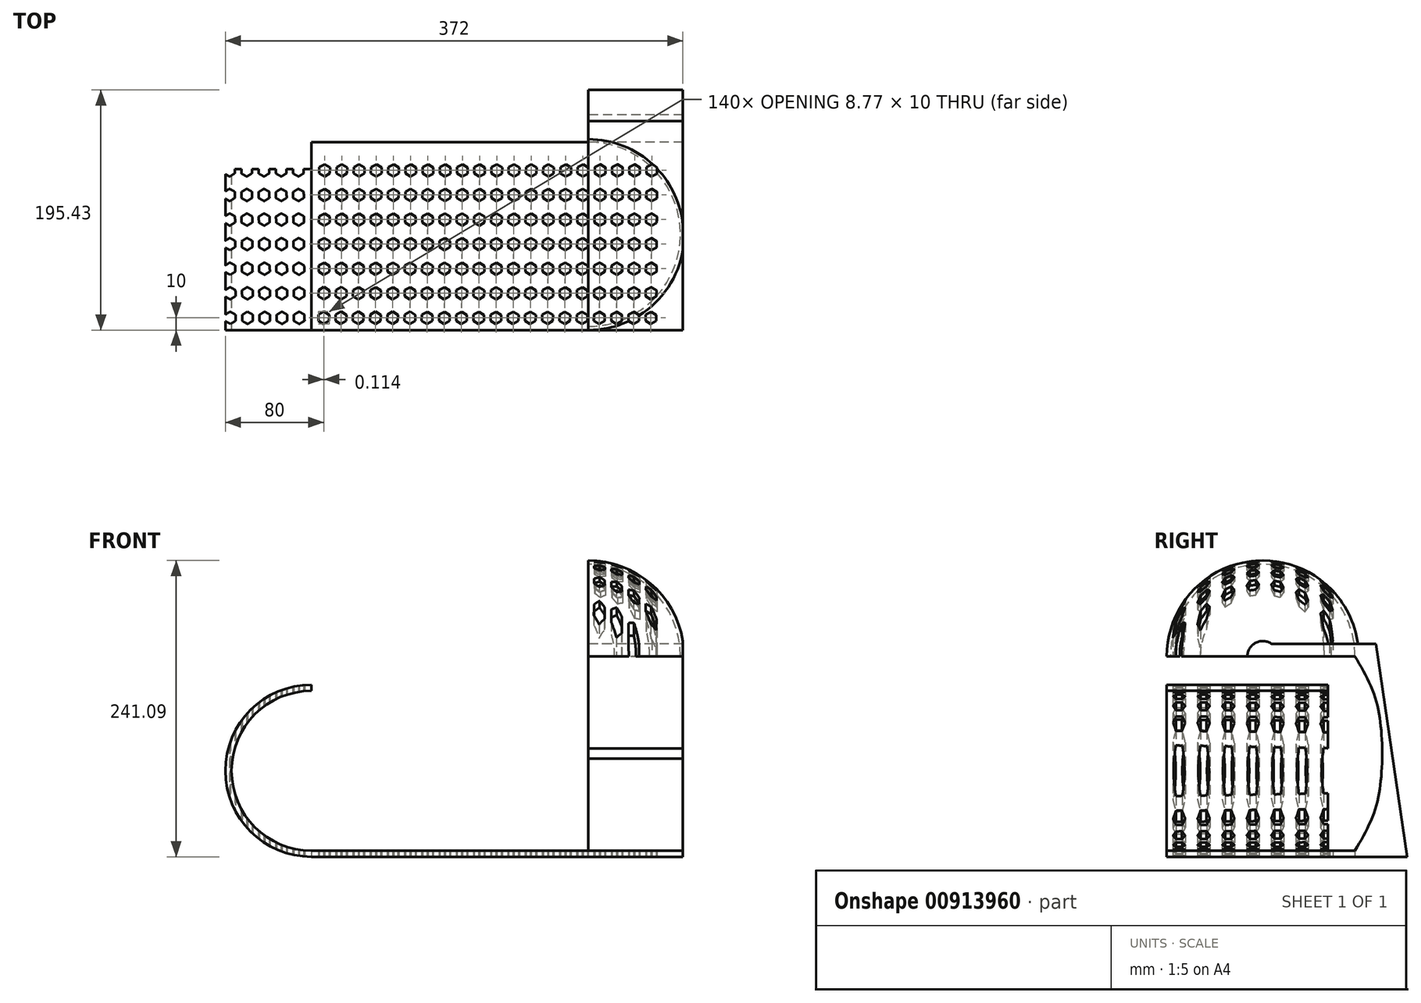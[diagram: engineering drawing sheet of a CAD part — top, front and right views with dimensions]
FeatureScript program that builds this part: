
annotation { "Feature Type Name" : "Feature", "Feature Type Description" : "" }
export const myFeature = defineFeature(function(context is Context, id is Id, definition is map)
    precondition{}
    {
        {
            var Q0;
            Q0=qCreatedBy(makeId("Right.planeOp"),FACE);
            var sketch = newSketch(context, id + "F0", { "sketchPlane" : qUnion([Q0])});
            skArc(sketch, "E0", {"start": v(75, 0) * mm, "mid": v(0, 75) * mm, "end": v(-75, 0) * mm});
            skLineSegment(sketch, "E1", {"start": v(-75, 0) * mm, "end": v(75, 0) * mm, "construction": true});
            skArc(sketch, "E2.0", {"start": v(78, 0) * mm, "mid": v(0, 78) * mm, "end": v(-78, 0) * mm});
            skLineSegment(sketch, "E3", {"start": v(-78, 0) * mm, "end": v(-75, 0) * mm});
            skLineSegment(sketch, "E4", {"start": v(75, 0) * mm, "end": v(78, 0) * mm});
            skSolve(sketch);
        }
        {
            var Q0;
            Q0=makeQuery(id+"F0.imprint","IMPRINT",FACE,{"disambiguationData":[TD([[makeQuery(id+"F0.imprint","IMPRINT",EDGE,{"derivedFrom":sQuery(id+"F0.wireOp",EDGE,"E0")}),-1.0]])]});
            var Q1;
            Q1=sQuery(id+"F0.wireOp",EDGE,"E1");
            revolve(context, id + "F1", {"surfaceOperationType" : NewSurfaceOperationType.NEW, "entities" : qUnion([Q0]), "axis" : qUnion([Q1]), "revolveType" : RevolveType.ONE_DIRECTION, "angle" : 90 * degree});
        }
        {
            var Q0;
            Q0=qCreatedBy(makeId("Right.planeOp"),FACE);
            var sketch = newSketch(context, id + "F2", { "sketchPlane" : qUnion([Q0])});
            skLineSegment(sketch, "E5.0.0", {"start": v(75, 0) * mm, "end": v(-75, 0) * mm});
            skArc(sketch, "E6", {"start": v(75, 0) * mm, "mid": v(0, 75) * mm, "end": v(-75, 0) * mm, "construction": true});
            skFitSpline(sketch, "E7", {"points": [v(75, 0) * mm, v(91.76, -34.74) * mm, v(97.2, -75) * mm], "startDerivative": vector(40.46, -68.62) * mm, "endDerivative": vector(3.7, -86.55) * mm});
            skLineSegment(sketch, "E8", {"start": v(92, 10) * mm, "end": v(105.08, -79.04) * mm});
            skLineSegment(sketch, "E9", {"start": v(105.08, -79.04) * mm, "end": v(97.2, -75) * mm});
            skArc(sketch, "E10.0.0", {"start": v(78, 0) * mm, "mid": v(0, 78) * mm, "end": v(-78, 0) * mm, "construction": true});
            skLineSegment(sketch, "E10.0.1", {"start": v(-78, 0) * mm, "end": v(78, 0) * mm});
            skLineSegment(sketch, "E11", {"start": v(-78, 0) * mm, "end": v(-78, 10) * mm});
            skLineSegment(sketch, "E12", {"start": v(-78, 10) * mm, "end": v(92, 10) * mm});
            skLineSegment(sketch, "E13", {"start": v(75, 0) * mm, "end": v(75, 10) * mm});
            skLineSegment(sketch, "E14", {"start": v(105.08, -79.04) * mm, "end": v(-109.24, -79.04) * mm, "construction": true});
            skFitSpline(sketch, "E15.MirrorCS", {"points": [v(75, -158.09) * mm, v(91.76, -123.35) * mm, v(97.2, -83.09) * mm], "startDerivative": vector(40.46, 68.62) * mm, "endDerivative": vector(3.7, 86.55) * mm});
            skLineSegment(sketch, "E16", {"start": v(105.08, -79.04) * mm, "end": v(117.43, -163.09) * mm});
            skLineSegment(sketch, "E17", {"start": v(117.43, -163.09) * mm, "end": v(-78, -163.09) * mm});
            skLineSegment(sketch, "E18", {"start": v(-78, -163.09) * mm, "end": v(-78, 0) * mm, "construction": true});
            skLineSegment(sketch, "E19", {"start": v(75, -158.09) * mm, "end": v(-78, -158.09) * mm});
            skLineSegment(sketch, "E20", {"start": v(-78, -158.09) * mm, "end": v(-78, -163.09) * mm});
            skLineSegment(sketch, "E21", {"start": v(97.2, -83.09) * mm, "end": v(97.2, -75) * mm});
            skLineSegment(sketch, "E22", {"start": v(75, -158.09) * mm, "end": v(75, -163.09) * mm});
            skSolve(sketch);
        }
        {
            var Q0;
            {var subQ1=sQuery(id+"F2.wireOp",EDGE,"E7");Q0=makeQuery(id+"F2.imprint","IMPRINT",FACE,{"disambiguationData":[TD([[makeQuery(id+"F2.imprint","IMPRINT",EDGE,{"derivedFrom":subQ1}),1.0]])]});}
            extrude(context, id + "F3", {"entities" : qUnion([Q0]), "depth" : 150 * mm, "offsetDistance" : 25 * mm, "hasSecondDirection" : true, "secondDirectionOppositeDirection" : true, "secondDirectionDepth" : 0 * mm});
        }
        {
            var Q0;
            Q0=makeQuery(id+"F2.imprint","IMPRINT",FACE,{"disambiguationData":[TD([[makeQuery(id+"F2.imprint","IMPRINT",EDGE,{"derivedFrom":sQuery(id+"F2.wireOp",EDGE,"E9")}),1.0]])]});
            var Q1;
            Q1=makeQuery(id+"F2.imprint","IMPRINT",FACE,{"disambiguationData":[TD([[makeQuery(id+"F2.imprint","IMPRINT",EDGE,{"derivedFrom":sQuery(id+"F2.wireOp",EDGE,"E19")}),1.0]])]});
            extrude(context, id + "F4", {"entities" : qUnion([Q0, Q1]), "operationType" : NewBodyOperationType.ADD, "depth" : 77 * mm, "offsetDistance" : 25 * mm});
        }
        {
            var Q0;
            Q0=makeQuery(id+"F3.opExtrude","CAP_FACE",FACE,{"disambiguationData":[OSD([sQuery(id+"F2.wireOp",EDGE,"E7"),sQuery(id+"F2.wireOp",EDGE,"E8"),sQuery(id+"F2.wireOp",EDGE,"E9"),sQuery(id+"F2.wireOp",EDGE,"E12"),sQuery(id+"F2.wireOp",EDGE,"E13")])],"isStart":false});
            var sketch = newSketch(context, id + "F5", { "sketchPlane" : qUnion([Q0])});
            skLineSegment(sketch, "E23.bottom", {"start": v(0, 0) * mm, "end": v(75, 0) * mm});
            skLineSegment(sketch, "E23.top", {"start": v(0, 10) * mm, "end": v(75, 10) * mm});
            skLineSegment(sketch, "E23.left", {"start": v(0, 0) * mm, "end": v(0, 10) * mm});
            skLineSegment(sketch, "E23.right", {"start": v(75, 0) * mm, "end": v(75, 10) * mm});
            skSolve(sketch);
        }
        {
            var Q0;
            Q0=makeQuery(id+"F5.imprint","IMPRINT",FACE,{"disambiguationData":[TD([[makeQuery(id+"F5.imprint","IMPRINT",EDGE,{"derivedFrom":sQuery(id+"F5.wireOp",EDGE,"E23.bottom")}),1.0]])]});
            extrude(context, id + "F6", {"entities" : qUnion([Q0]), "operationType" : NewBodyOperationType.ADD, "endBound" : BoundingType.UP_TO_NEXT, "oppositeDirection" : true, "depth" : 25 * mm, "offsetDistance" : 25 * mm});
        }
        {
            var Q0;
            Q0=makeQuery(id+"F4.opExtrude","CAP_FACE",FACE,{"disambiguationData":[OSD([sQuery(id+"F2.wireOp",EDGE,"E9"),sQuery(id+"F2.wireOp",EDGE,"E15.MirrorCS"),sQuery(id+"F2.wireOp",EDGE,"E16"),sQuery(id+"F2.wireOp",EDGE,"E17"),sQuery(id+"F2.wireOp",EDGE,"E19"),sQuery(id+"F2.wireOp",EDGE,"E20"),sQuery(id+"F2.wireOp",EDGE,"E21")])],"isStart":true});
            var sketch = newSketch(context, id + "F7", { "sketchPlane" : qUnion([Q0])});
            skLineSegment(sketch, "E24.bottom", {"start": v(-75, -158.09) * mm, "end": v(78, -158.09) * mm});
            skLineSegment(sketch, "E24.top", {"start": v(-75, -163.09) * mm, "end": v(78, -163.09) * mm});
            skLineSegment(sketch, "E24.left", {"start": v(-75, -158.09) * mm, "end": v(-75, -163.09) * mm});
            skLineSegment(sketch, "E24.right", {"start": v(78, -158.09) * mm, "end": v(78, -163.09) * mm});
            skSolve(sketch);
        }
        {
            var Q0;
            Q0=makeQuery(id+"F7.imprint","IMPRINT",FACE,{"disambiguationData":[TD([[makeQuery(id+"F7.imprint","IMPRINT",EDGE,{"derivedFrom":sQuery(id+"F7.wireOp",EDGE,"E24.bottom")}),-1.0]])]});
            extrude(context, id + "F8", {"entities" : qUnion([Q0]), "operationType" : NewBodyOperationType.ADD, "depth" : 225 * mm, "offsetDistance" : 25 * mm});
        }
        {
            var Q0;
            Q0=makeQuery(id+"F8.boolean.opBoolean","MERGE",FACE,{"derivedFrom":[makeQuery(id+"F4.opExtrude","SWEPT_FACE",FACE,{"disambiguationData":[OSD([sQuery(id+"F2.wireOp",EDGE,"E20")])]}),makeQuery(id+"F8.opExtrude","SWEPT_FACE",FACE,{"disambiguationData":[OSD([sQuery(id+"F7.wireOp",EDGE,"E24.right")])]})]});
            var sketch = newSketch(context, id + "F9", { "sketchPlane" : qUnion([Q0])});
            skArc(sketch, "E25", {"start": v(-225, -28.09) * mm, "mid": v(-290, -93.09) * mm, "end": v(-225, -158.09) * mm});
            skArc(sketch, "E26.0", {"start": v(-225, -23.09) * mm, "mid": v(-295, -93.09) * mm, "end": v(-225, -163.09) * mm});
            skLineSegment(sketch, "E27", {"start": v(-225, -28.09) * mm, "end": v(-225, -23.09) * mm});
            skSolve(sketch);
        }
        {
            var Q0;
            Q0 = qSketchRegion(id + "F9", true);
            var Q1;
            Q1=makeQuery(id+"F9.imprint","IMPRINT",FACE,{"disambiguationData":[TD([[makeQuery(id+"F9.imprint","IMPRINT",EDGE,{"derivedFrom":sQuery(id+"F9.wireOp",EDGE,"E25")}),-1.0]])]});
            extrude(context, id + "F10", {"entities" : qUnion([Q0, Q1]), "operationType" : NewBodyOperationType.ADD, "oppositeDirection" : true, "depth" : 131 * mm, "offsetDistance" : 25 * mm});
        }
        {
            var Q0;
            Q0=makeQuery(id+"F8.boolean.opBoolean","MERGE",FACE,{"derivedFrom":[makeQuery(id+"F4.opExtrude","SWEPT_FACE",FACE,{"disambiguationData":[OSD([sQuery(id+"F2.wireOp",EDGE,"E17")])]}),makeQuery(id+"F8.opExtrude","SWEPT_FACE",FACE,{"disambiguationData":[OSD([sQuery(id+"F7.wireOp",EDGE,"E24.top")])]})]});
            var sketch = newSketch(context, id + "F11", { "sketchPlane" : qUnion([Q0])});
            skCircle(sketch, "E28.cCircle", {"center": v(-215, 68) * mm, "radius": 4.33 * mm, "construction": true});
            skLineSegment(sketch, "E28.0", {"start": v(-210.61, 65.6) * mm, "end": v(-214.89, 63) * mm});
            skLineSegment(sketch, "E28.1", {"start": v(-214.89, 63) * mm, "end": v(-219.27, 65.4) * mm});
            skLineSegment(sketch, "E28.2", {"start": v(-219.27, 65.4) * mm, "end": v(-219.39, 70.4) * mm});
            skLineSegment(sketch, "E28.3", {"start": v(-219.39, 70.4) * mm, "end": v(-215.11, 73) * mm});
            skLineSegment(sketch, "E28.4", {"start": v(-215.11, 73) * mm, "end": v(-210.73, 70.6) * mm});
            skLineSegment(sketch, "E28.5", {"start": v(-210.73, 70.6) * mm, "end": v(-210.61, 65.6) * mm});
            skPoint(sketch, "E28.0.midPoint", {"position": v(-212.75, 64.3) * mm});
            skLineSegment(sketch, "E29.0.1.0", {"start": v(-215, 53) * mm, "end": v(-210.61, 50.6) * mm});
            skLineSegment(sketch, "E29.0.1.1", {"start": v(-210.61, 50.6) * mm, "end": v(-210.5, 45.6) * mm});
            skLineSegment(sketch, "E29.0.1.2", {"start": v(-219.27, 50.4) * mm, "end": v(-215, 53) * mm});
            skLineSegment(sketch, "E29.0.1.3", {"start": v(-219.16, 45.4) * mm, "end": v(-219.27, 50.4) * mm});
            skLineSegment(sketch, "E29.0.1.4", {"start": v(-214.77, 43) * mm, "end": v(-219.16, 45.4) * mm});
            skLineSegment(sketch, "E29.0.1.5", {"start": v(-210.5, 45.6) * mm, "end": v(-214.77, 43) * mm});
            skLineSegment(sketch, "E29.0.2.0", {"start": v(-214.89, 33) * mm, "end": v(-210.5, 30.6) * mm});
            skLineSegment(sketch, "E29.0.2.1", {"start": v(-210.5, 30.6) * mm, "end": v(-210.38, 25.6) * mm});
            skLineSegment(sketch, "E29.0.2.2", {"start": v(-219.16, 30.4) * mm, "end": v(-214.89, 33) * mm});
            skLineSegment(sketch, "E29.0.2.3", {"start": v(-219.04, 25.4) * mm, "end": v(-219.16, 30.4) * mm});
            skLineSegment(sketch, "E29.0.2.4", {"start": v(-214.66, 23) * mm, "end": v(-219.04, 25.4) * mm});
            skLineSegment(sketch, "E29.0.2.5", {"start": v(-210.38, 25.6) * mm, "end": v(-214.66, 23) * mm});
            skLineSegment(sketch, "E29.0.3.0", {"start": v(-214.77, 13) * mm, "end": v(-210.38, 10.6) * mm});
            skLineSegment(sketch, "E29.0.3.1", {"start": v(-210.38, 10.6) * mm, "end": v(-210.27, 5.6) * mm});
            skLineSegment(sketch, "E29.0.3.2", {"start": v(-219.04, 10.4) * mm, "end": v(-214.77, 13) * mm});
            skLineSegment(sketch, "E29.0.3.3", {"start": v(-218.93, 5.4) * mm, "end": v(-219.04, 10.4) * mm});
            skLineSegment(sketch, "E29.0.3.4", {"start": v(-214.54, 3) * mm, "end": v(-218.93, 5.4) * mm});
            skLineSegment(sketch, "E29.0.3.5", {"start": v(-210.27, 5.6) * mm, "end": v(-214.54, 3) * mm});
            skLineSegment(sketch, "E29.0.4.0", {"start": v(-214.66, -7) * mm, "end": v(-210.27, -9.4) * mm});
            skLineSegment(sketch, "E29.0.4.1", {"start": v(-210.27, -9.4) * mm, "end": v(-210.16, -14.4) * mm});
            skLineSegment(sketch, "E29.0.4.2", {"start": v(-218.93, -9.6) * mm, "end": v(-214.66, -7) * mm});
            skLineSegment(sketch, "E29.0.4.3", {"start": v(-218.81, -14.6) * mm, "end": v(-218.93, -9.6) * mm});
            skLineSegment(sketch, "E29.0.4.4", {"start": v(-214.43, -17) * mm, "end": v(-218.81, -14.6) * mm});
            skLineSegment(sketch, "E29.0.4.5", {"start": v(-210.16, -14.4) * mm, "end": v(-214.43, -17) * mm});
            skLineSegment(sketch, "E29.0.5.0", {"start": v(-214.54, -27) * mm, "end": v(-210.16, -29.4) * mm});
            skLineSegment(sketch, "E29.0.5.1", {"start": v(-210.16, -29.4) * mm, "end": v(-210.04, -34.4) * mm});
            skLineSegment(sketch, "E29.0.5.2", {"start": v(-218.81, -29.6) * mm, "end": v(-214.54, -27) * mm});
            skLineSegment(sketch, "E29.0.5.3", {"start": v(-218.7, -34.6) * mm, "end": v(-218.81, -29.6) * mm});
            skLineSegment(sketch, "E29.0.5.4", {"start": v(-214.31, -37) * mm, "end": v(-218.7, -34.6) * mm});
            skLineSegment(sketch, "E29.0.5.5", {"start": v(-210.04, -34.4) * mm, "end": v(-214.31, -37) * mm});
            skLineSegment(sketch, "E29.0.6.0", {"start": v(-214.43, -47) * mm, "end": v(-210.04, -49.4) * mm});
            skLineSegment(sketch, "E29.0.6.1", {"start": v(-210.04, -49.4) * mm, "end": v(-209.93, -54.4) * mm});
            skLineSegment(sketch, "E29.0.6.2", {"start": v(-218.7, -49.6) * mm, "end": v(-214.43, -47) * mm});
            skLineSegment(sketch, "E29.0.6.3", {"start": v(-218.59, -54.6) * mm, "end": v(-218.7, -49.6) * mm});
            skLineSegment(sketch, "E29.0.6.4", {"start": v(-214.2, -57) * mm, "end": v(-218.59, -54.6) * mm});
            skLineSegment(sketch, "E29.0.6.5", {"start": v(-209.93, -54.4) * mm, "end": v(-214.2, -57) * mm});
            skLineSegment(sketch, "E29.1.0.0", {"start": v(-201.11, 73) * mm, "end": v(-196.73, 70.6) * mm});
            skLineSegment(sketch, "E29.1.0.1", {"start": v(-196.73, 70.6) * mm, "end": v(-196.61, 65.6) * mm});
            skLineSegment(sketch, "E29.1.0.2", {"start": v(-205.39, 70.4) * mm, "end": v(-201.11, 73) * mm});
            skLineSegment(sketch, "E29.1.0.3", {"start": v(-205.27, 65.4) * mm, "end": v(-205.39, 70.4) * mm});
            skLineSegment(sketch, "E29.1.0.4", {"start": v(-200.89, 63) * mm, "end": v(-205.27, 65.4) * mm});
            skLineSegment(sketch, "E29.1.0.5", {"start": v(-196.61, 65.6) * mm, "end": v(-200.89, 63) * mm});
            skLineSegment(sketch, "E29.1.1.0", {"start": v(-201, 53) * mm, "end": v(-196.61, 50.6) * mm});
            skLineSegment(sketch, "E29.1.1.1", {"start": v(-196.61, 50.6) * mm, "end": v(-196.5, 45.6) * mm});
            skLineSegment(sketch, "E29.1.1.2", {"start": v(-205.27, 50.4) * mm, "end": v(-201, 53) * mm});
            skLineSegment(sketch, "E29.1.1.3", {"start": v(-205.16, 45.4) * mm, "end": v(-205.27, 50.4) * mm});
            skLineSegment(sketch, "E29.1.1.4", {"start": v(-200.77, 43) * mm, "end": v(-205.16, 45.4) * mm});
            skLineSegment(sketch, "E29.1.1.5", {"start": v(-196.5, 45.6) * mm, "end": v(-200.77, 43) * mm});
            skLineSegment(sketch, "E29.1.2.0", {"start": v(-200.89, 33) * mm, "end": v(-196.5, 30.6) * mm});
            skLineSegment(sketch, "E29.1.2.1", {"start": v(-196.5, 30.6) * mm, "end": v(-196.38, 25.6) * mm});
            skLineSegment(sketch, "E29.1.2.2", {"start": v(-205.16, 30.4) * mm, "end": v(-200.89, 33) * mm});
            skLineSegment(sketch, "E29.1.2.3", {"start": v(-205.04, 25.4) * mm, "end": v(-205.16, 30.4) * mm});
            skLineSegment(sketch, "E29.1.2.4", {"start": v(-200.66, 23) * mm, "end": v(-205.04, 25.4) * mm});
            skLineSegment(sketch, "E29.1.2.5", {"start": v(-196.38, 25.6) * mm, "end": v(-200.66, 23) * mm});
            skLineSegment(sketch, "E29.1.3.0", {"start": v(-200.77, 13) * mm, "end": v(-196.38, 10.6) * mm});
            skLineSegment(sketch, "E29.1.3.1", {"start": v(-196.38, 10.6) * mm, "end": v(-196.27, 5.6) * mm});
            skLineSegment(sketch, "E29.1.3.2", {"start": v(-205.04, 10.4) * mm, "end": v(-200.77, 13) * mm});
            skLineSegment(sketch, "E29.1.3.3", {"start": v(-204.93, 5.4) * mm, "end": v(-205.04, 10.4) * mm});
            skLineSegment(sketch, "E29.1.3.4", {"start": v(-200.54, 3) * mm, "end": v(-204.93, 5.4) * mm});
            skLineSegment(sketch, "E29.1.3.5", {"start": v(-196.27, 5.6) * mm, "end": v(-200.54, 3) * mm});
            skLineSegment(sketch, "E29.1.4.0", {"start": v(-200.66, -7) * mm, "end": v(-196.27, -9.4) * mm});
            skLineSegment(sketch, "E29.1.4.1", {"start": v(-196.27, -9.4) * mm, "end": v(-196.16, -14.4) * mm});
            skLineSegment(sketch, "E29.1.4.2", {"start": v(-204.93, -9.6) * mm, "end": v(-200.66, -7) * mm});
            skLineSegment(sketch, "E29.1.4.3", {"start": v(-204.81, -14.6) * mm, "end": v(-204.93, -9.6) * mm});
            skLineSegment(sketch, "E29.1.4.4", {"start": v(-200.43, -17) * mm, "end": v(-204.81, -14.6) * mm});
            skLineSegment(sketch, "E29.1.4.5", {"start": v(-196.16, -14.4) * mm, "end": v(-200.43, -17) * mm});
            skLineSegment(sketch, "E29.1.5.0", {"start": v(-200.54, -27) * mm, "end": v(-196.16, -29.4) * mm});
            skLineSegment(sketch, "E29.1.5.1", {"start": v(-196.16, -29.4) * mm, "end": v(-196.04, -34.4) * mm});
            skLineSegment(sketch, "E29.1.5.2", {"start": v(-204.81, -29.6) * mm, "end": v(-200.54, -27) * mm});
            skLineSegment(sketch, "E29.1.5.3", {"start": v(-204.7, -34.6) * mm, "end": v(-204.81, -29.6) * mm});
            skLineSegment(sketch, "E29.1.5.4", {"start": v(-200.31, -37) * mm, "end": v(-204.7, -34.6) * mm});
            skLineSegment(sketch, "E29.1.5.5", {"start": v(-196.04, -34.4) * mm, "end": v(-200.31, -37) * mm});
            skLineSegment(sketch, "E29.1.6.0", {"start": v(-200.43, -47) * mm, "end": v(-196.04, -49.4) * mm});
            skLineSegment(sketch, "E29.1.6.1", {"start": v(-196.04, -49.4) * mm, "end": v(-195.93, -54.4) * mm});
            skLineSegment(sketch, "E29.1.6.2", {"start": v(-204.7, -49.6) * mm, "end": v(-200.43, -47) * mm});
            skLineSegment(sketch, "E29.1.6.3", {"start": v(-204.59, -54.59) * mm, "end": v(-204.7, -49.6) * mm});
            skLineSegment(sketch, "E29.1.6.4", {"start": v(-200.2, -56.99) * mm, "end": v(-204.59, -54.59) * mm});
            skLineSegment(sketch, "E29.1.6.5", {"start": v(-195.93, -54.4) * mm, "end": v(-200.2, -56.99) * mm});
            skLineSegment(sketch, "E29.2.0.0", {"start": v(-187.11, 73) * mm, "end": v(-182.73, 70.6) * mm});
            skLineSegment(sketch, "E29.2.0.1", {"start": v(-182.73, 70.6) * mm, "end": v(-182.61, 65.6) * mm});
            skLineSegment(sketch, "E29.2.0.2", {"start": v(-191.39, 70.4) * mm, "end": v(-187.11, 73) * mm});
            skLineSegment(sketch, "E29.2.0.3", {"start": v(-191.27, 65.4) * mm, "end": v(-191.39, 70.4) * mm});
            skLineSegment(sketch, "E29.2.0.4", {"start": v(-186.89, 63) * mm, "end": v(-191.27, 65.4) * mm});
            skLineSegment(sketch, "E29.2.0.5", {"start": v(-182.61, 65.6) * mm, "end": v(-186.89, 63) * mm});
            skLineSegment(sketch, "E29.2.1.0", {"start": v(-187, 53) * mm, "end": v(-182.61, 50.6) * mm});
            skLineSegment(sketch, "E29.2.1.1", {"start": v(-182.61, 50.6) * mm, "end": v(-182.5, 45.6) * mm});
            skLineSegment(sketch, "E29.2.1.2", {"start": v(-191.27, 50.4) * mm, "end": v(-187, 53) * mm});
            skLineSegment(sketch, "E29.2.1.3", {"start": v(-191.16, 45.4) * mm, "end": v(-191.27, 50.4) * mm});
            skLineSegment(sketch, "E29.2.1.4", {"start": v(-186.77, 43) * mm, "end": v(-191.16, 45.4) * mm});
            skLineSegment(sketch, "E29.2.1.5", {"start": v(-182.5, 45.6) * mm, "end": v(-186.77, 43) * mm});
            skLineSegment(sketch, "E29.2.2.0", {"start": v(-186.89, 33) * mm, "end": v(-182.5, 30.6) * mm});
            skLineSegment(sketch, "E29.2.2.1", {"start": v(-182.5, 30.6) * mm, "end": v(-182.38, 25.6) * mm});
            skLineSegment(sketch, "E29.2.2.2", {"start": v(-191.16, 30.4) * mm, "end": v(-186.89, 33) * mm});
            skLineSegment(sketch, "E29.2.2.3", {"start": v(-191.04, 25.4) * mm, "end": v(-191.16, 30.4) * mm});
            skLineSegment(sketch, "E29.2.2.4", {"start": v(-186.66, 23) * mm, "end": v(-191.04, 25.4) * mm});
            skLineSegment(sketch, "E29.2.2.5", {"start": v(-182.38, 25.6) * mm, "end": v(-186.66, 23) * mm});
            skLineSegment(sketch, "E29.2.3.0", {"start": v(-186.77, 13) * mm, "end": v(-182.38, 10.6) * mm});
            skLineSegment(sketch, "E29.2.3.1", {"start": v(-182.38, 10.6) * mm, "end": v(-182.27, 5.6) * mm});
            skLineSegment(sketch, "E29.2.3.2", {"start": v(-191.04, 10.4) * mm, "end": v(-186.77, 13) * mm});
            skLineSegment(sketch, "E29.2.3.3", {"start": v(-190.93, 5.4) * mm, "end": v(-191.04, 10.4) * mm});
            skLineSegment(sketch, "E29.2.3.4", {"start": v(-186.54, 3) * mm, "end": v(-190.93, 5.4) * mm});
            skLineSegment(sketch, "E29.2.3.5", {"start": v(-182.27, 5.6) * mm, "end": v(-186.54, 3) * mm});
            skLineSegment(sketch, "E29.2.4.0", {"start": v(-186.66, -7) * mm, "end": v(-182.27, -9.4) * mm});
            skLineSegment(sketch, "E29.2.4.1", {"start": v(-182.27, -9.4) * mm, "end": v(-182.16, -14.4) * mm});
            skLineSegment(sketch, "E29.2.4.2", {"start": v(-190.93, -9.6) * mm, "end": v(-186.66, -7) * mm});
            skLineSegment(sketch, "E29.2.4.3", {"start": v(-190.81, -14.6) * mm, "end": v(-190.93, -9.6) * mm});
            skLineSegment(sketch, "E29.2.4.4", {"start": v(-186.43, -17) * mm, "end": v(-190.81, -14.6) * mm});
            skLineSegment(sketch, "E29.2.4.5", {"start": v(-182.16, -14.4) * mm, "end": v(-186.43, -17) * mm});
            skLineSegment(sketch, "E29.2.5.0", {"start": v(-186.54, -27) * mm, "end": v(-182.16, -29.4) * mm});
            skLineSegment(sketch, "E29.2.5.1", {"start": v(-182.16, -29.4) * mm, "end": v(-182.04, -34.4) * mm});
            skLineSegment(sketch, "E29.2.5.2", {"start": v(-190.81, -29.6) * mm, "end": v(-186.54, -27) * mm});
            skLineSegment(sketch, "E29.2.5.3", {"start": v(-190.7, -34.6) * mm, "end": v(-190.81, -29.6) * mm});
            skLineSegment(sketch, "E29.2.5.4", {"start": v(-186.31, -37) * mm, "end": v(-190.7, -34.6) * mm});
            skLineSegment(sketch, "E29.2.5.5", {"start": v(-182.04, -34.4) * mm, "end": v(-186.31, -37) * mm});
            skLineSegment(sketch, "E29.2.6.0", {"start": v(-186.43, -47) * mm, "end": v(-182.04, -49.4) * mm});
            skLineSegment(sketch, "E29.2.6.1", {"start": v(-182.04, -49.4) * mm, "end": v(-181.93, -54.4) * mm});
            skLineSegment(sketch, "E29.2.6.2", {"start": v(-190.7, -49.6) * mm, "end": v(-186.43, -47) * mm});
            skLineSegment(sketch, "E29.2.6.3", {"start": v(-190.59, -54.59) * mm, "end": v(-190.7, -49.6) * mm});
            skLineSegment(sketch, "E29.2.6.4", {"start": v(-186.2, -56.99) * mm, "end": v(-190.59, -54.59) * mm});
            skLineSegment(sketch, "E29.2.6.5", {"start": v(-181.93, -54.4) * mm, "end": v(-186.2, -56.99) * mm});
            skLineSegment(sketch, "E29.3.0.0", {"start": v(-173.11, 73) * mm, "end": v(-168.73, 70.6) * mm});
            skLineSegment(sketch, "E29.3.0.1", {"start": v(-168.73, 70.6) * mm, "end": v(-168.61, 65.6) * mm});
            skLineSegment(sketch, "E29.3.0.2", {"start": v(-177.39, 70.4) * mm, "end": v(-173.11, 73) * mm});
            skLineSegment(sketch, "E29.3.0.3", {"start": v(-177.27, 65.4) * mm, "end": v(-177.39, 70.4) * mm});
            skLineSegment(sketch, "E29.3.0.4", {"start": v(-172.89, 63) * mm, "end": v(-177.27, 65.4) * mm});
            skLineSegment(sketch, "E29.3.0.5", {"start": v(-168.61, 65.6) * mm, "end": v(-172.89, 63) * mm});
            skLineSegment(sketch, "E29.3.1.0", {"start": v(-173, 53) * mm, "end": v(-168.61, 50.6) * mm});
            skLineSegment(sketch, "E29.3.1.1", {"start": v(-168.61, 50.6) * mm, "end": v(-168.5, 45.6) * mm});
            skLineSegment(sketch, "E29.3.1.2", {"start": v(-177.27, 50.4) * mm, "end": v(-173, 53) * mm});
            skLineSegment(sketch, "E29.3.1.3", {"start": v(-177.16, 45.4) * mm, "end": v(-177.27, 50.4) * mm});
            skLineSegment(sketch, "E29.3.1.4", {"start": v(-172.77, 43) * mm, "end": v(-177.16, 45.4) * mm});
            skLineSegment(sketch, "E29.3.1.5", {"start": v(-168.5, 45.6) * mm, "end": v(-172.77, 43) * mm});
            skLineSegment(sketch, "E29.3.2.0", {"start": v(-172.89, 33) * mm, "end": v(-168.5, 30.6) * mm});
            skLineSegment(sketch, "E29.3.2.1", {"start": v(-168.5, 30.6) * mm, "end": v(-168.38, 25.6) * mm});
            skLineSegment(sketch, "E29.3.2.2", {"start": v(-177.16, 30.4) * mm, "end": v(-172.89, 33) * mm});
            skLineSegment(sketch, "E29.3.2.3", {"start": v(-177.04, 25.4) * mm, "end": v(-177.16, 30.4) * mm});
            skLineSegment(sketch, "E29.3.2.4", {"start": v(-172.66, 23) * mm, "end": v(-177.04, 25.4) * mm});
            skLineSegment(sketch, "E29.3.2.5", {"start": v(-168.38, 25.6) * mm, "end": v(-172.66, 23) * mm});
            skLineSegment(sketch, "E29.3.3.0", {"start": v(-172.77, 13) * mm, "end": v(-168.38, 10.6) * mm});
            skLineSegment(sketch, "E29.3.3.1", {"start": v(-168.38, 10.6) * mm, "end": v(-168.27, 5.6) * mm});
            skLineSegment(sketch, "E29.3.3.2", {"start": v(-177.04, 10.4) * mm, "end": v(-172.77, 13) * mm});
            skLineSegment(sketch, "E29.3.3.3", {"start": v(-176.93, 5.4) * mm, "end": v(-177.04, 10.4) * mm});
            skLineSegment(sketch, "E29.3.3.4", {"start": v(-172.54, 3) * mm, "end": v(-176.93, 5.4) * mm});
            skLineSegment(sketch, "E29.3.3.5", {"start": v(-168.27, 5.6) * mm, "end": v(-172.54, 3) * mm});
            skLineSegment(sketch, "E29.3.4.0", {"start": v(-172.66, -7) * mm, "end": v(-168.27, -9.4) * mm});
            skLineSegment(sketch, "E29.3.4.1", {"start": v(-168.27, -9.4) * mm, "end": v(-168.16, -14.4) * mm});
            skLineSegment(sketch, "E29.3.4.2", {"start": v(-176.93, -9.6) * mm, "end": v(-172.66, -7) * mm});
            skLineSegment(sketch, "E29.3.4.3", {"start": v(-176.81, -14.6) * mm, "end": v(-176.93, -9.6) * mm});
            skLineSegment(sketch, "E29.3.4.4", {"start": v(-172.43, -17) * mm, "end": v(-176.81, -14.6) * mm});
            skLineSegment(sketch, "E29.3.4.5", {"start": v(-168.16, -14.4) * mm, "end": v(-172.43, -17) * mm});
            skLineSegment(sketch, "E29.3.5.0", {"start": v(-172.54, -27) * mm, "end": v(-168.16, -29.4) * mm});
            skLineSegment(sketch, "E29.3.5.1", {"start": v(-168.16, -29.4) * mm, "end": v(-168.04, -34.4) * mm});
            skLineSegment(sketch, "E29.3.5.2", {"start": v(-176.81, -29.6) * mm, "end": v(-172.54, -27) * mm});
            skLineSegment(sketch, "E29.3.5.3", {"start": v(-176.7, -34.59) * mm, "end": v(-176.81, -29.6) * mm});
            skLineSegment(sketch, "E29.3.5.4", {"start": v(-172.31, -36.99) * mm, "end": v(-176.7, -34.59) * mm});
            skLineSegment(sketch, "E29.3.5.5", {"start": v(-168.04, -34.4) * mm, "end": v(-172.31, -36.99) * mm});
            skLineSegment(sketch, "E29.3.6.0", {"start": v(-172.43, -47) * mm, "end": v(-168.04, -49.4) * mm});
            skLineSegment(sketch, "E29.3.6.1", {"start": v(-168.04, -49.4) * mm, "end": v(-167.93, -54.39) * mm});
            skLineSegment(sketch, "E29.3.6.2", {"start": v(-176.7, -49.59) * mm, "end": v(-172.43, -47) * mm});
            skLineSegment(sketch, "E29.3.6.3", {"start": v(-176.59, -54.59) * mm, "end": v(-176.7, -49.59) * mm});
            skLineSegment(sketch, "E29.3.6.4", {"start": v(-172.2, -56.99) * mm, "end": v(-176.59, -54.59) * mm});
            skLineSegment(sketch, "E29.3.6.5", {"start": v(-167.93, -54.39) * mm, "end": v(-172.2, -56.99) * mm});
            skLineSegment(sketch, "E29.4.0.0", {"start": v(-159.11, 73) * mm, "end": v(-154.73, 70.6) * mm});
            skLineSegment(sketch, "E29.4.0.1", {"start": v(-154.73, 70.6) * mm, "end": v(-154.61, 65.6) * mm});
            skLineSegment(sketch, "E29.4.0.2", {"start": v(-163.39, 70.4) * mm, "end": v(-159.11, 73) * mm});
            skLineSegment(sketch, "E29.4.0.3", {"start": v(-163.27, 65.4) * mm, "end": v(-163.39, 70.4) * mm});
            skLineSegment(sketch, "E29.4.0.4", {"start": v(-158.89, 63) * mm, "end": v(-163.27, 65.4) * mm});
            skLineSegment(sketch, "E29.4.0.5", {"start": v(-154.61, 65.6) * mm, "end": v(-158.89, 63) * mm});
            skLineSegment(sketch, "E29.4.1.0", {"start": v(-159, 53) * mm, "end": v(-154.61, 50.6) * mm});
            skLineSegment(sketch, "E29.4.1.1", {"start": v(-154.61, 50.6) * mm, "end": v(-154.5, 45.6) * mm});
            skLineSegment(sketch, "E29.4.1.2", {"start": v(-163.27, 50.4) * mm, "end": v(-159, 53) * mm});
            skLineSegment(sketch, "E29.4.1.3", {"start": v(-163.16, 45.4) * mm, "end": v(-163.27, 50.4) * mm});
            skLineSegment(sketch, "E29.4.1.4", {"start": v(-158.77, 43) * mm, "end": v(-163.16, 45.4) * mm});
            skLineSegment(sketch, "E29.4.1.5", {"start": v(-154.5, 45.6) * mm, "end": v(-158.77, 43) * mm});
            skLineSegment(sketch, "E29.4.2.0", {"start": v(-158.89, 33) * mm, "end": v(-154.5, 30.6) * mm});
            skLineSegment(sketch, "E29.4.2.1", {"start": v(-154.5, 30.6) * mm, "end": v(-154.38, 25.6) * mm});
            skLineSegment(sketch, "E29.4.2.2", {"start": v(-163.16, 30.4) * mm, "end": v(-158.89, 33) * mm});
            skLineSegment(sketch, "E29.4.2.3", {"start": v(-163.04, 25.4) * mm, "end": v(-163.16, 30.4) * mm});
            skLineSegment(sketch, "E29.4.2.4", {"start": v(-158.66, 23) * mm, "end": v(-163.04, 25.4) * mm});
            skLineSegment(sketch, "E29.4.2.5", {"start": v(-154.38, 25.6) * mm, "end": v(-158.66, 23) * mm});
            skLineSegment(sketch, "E29.4.3.0", {"start": v(-158.77, 13) * mm, "end": v(-154.38, 10.6) * mm});
            skLineSegment(sketch, "E29.4.3.1", {"start": v(-154.38, 10.6) * mm, "end": v(-154.27, 5.6) * mm});
            skLineSegment(sketch, "E29.4.3.2", {"start": v(-163.04, 10.4) * mm, "end": v(-158.77, 13) * mm});
            skLineSegment(sketch, "E29.4.3.3", {"start": v(-162.93, 5.4) * mm, "end": v(-163.04, 10.4) * mm});
            skLineSegment(sketch, "E29.4.3.4", {"start": v(-158.54, 3) * mm, "end": v(-162.93, 5.4) * mm});
            skLineSegment(sketch, "E29.4.3.5", {"start": v(-154.27, 5.6) * mm, "end": v(-158.54, 3) * mm});
            skLineSegment(sketch, "E29.4.4.0", {"start": v(-158.66, -7) * mm, "end": v(-154.27, -9.4) * mm});
            skLineSegment(sketch, "E29.4.4.1", {"start": v(-154.27, -9.4) * mm, "end": v(-154.16, -14.4) * mm});
            skLineSegment(sketch, "E29.4.4.2", {"start": v(-162.93, -9.6) * mm, "end": v(-158.66, -7) * mm});
            skLineSegment(sketch, "E29.4.4.3", {"start": v(-162.81, -14.59) * mm, "end": v(-162.93, -9.6) * mm});
            skLineSegment(sketch, "E29.4.4.4", {"start": v(-158.43, -16.99) * mm, "end": v(-162.81, -14.59) * mm});
            skLineSegment(sketch, "E29.4.4.5", {"start": v(-154.16, -14.4) * mm, "end": v(-158.43, -16.99) * mm});
            skLineSegment(sketch, "E29.4.5.0", {"start": v(-158.54, -27) * mm, "end": v(-154.16, -29.4) * mm});
            skLineSegment(sketch, "E29.4.5.1", {"start": v(-154.16, -29.4) * mm, "end": v(-154.04, -34.4) * mm});
            skLineSegment(sketch, "E29.4.5.2", {"start": v(-162.81, -29.59) * mm, "end": v(-158.54, -27) * mm});
            skLineSegment(sketch, "E29.4.5.3", {"start": v(-162.7, -34.59) * mm, "end": v(-162.81, -29.59) * mm});
            skLineSegment(sketch, "E29.4.5.4", {"start": v(-158.31, -36.99) * mm, "end": v(-162.7, -34.59) * mm});
            skLineSegment(sketch, "E29.4.5.5", {"start": v(-154.04, -34.4) * mm, "end": v(-158.31, -36.99) * mm});
            skLineSegment(sketch, "E29.4.6.0", {"start": v(-158.43, -46.99) * mm, "end": v(-154.04, -49.4) * mm});
            skLineSegment(sketch, "E29.4.6.1", {"start": v(-154.04, -49.4) * mm, "end": v(-153.93, -54.39) * mm});
            skLineSegment(sketch, "E29.4.6.2", {"start": v(-162.7, -49.59) * mm, "end": v(-158.43, -46.99) * mm});
            skLineSegment(sketch, "E29.4.6.3", {"start": v(-162.59, -54.59) * mm, "end": v(-162.7, -49.59) * mm});
            skLineSegment(sketch, "E29.4.6.4", {"start": v(-158.2, -56.99) * mm, "end": v(-162.59, -54.59) * mm});
            skLineSegment(sketch, "E29.4.6.5", {"start": v(-153.93, -54.39) * mm, "end": v(-158.2, -56.99) * mm});
            skLineSegment(sketch, "E29.5.0.0", {"start": v(-145.11, 73) * mm, "end": v(-140.73, 70.6) * mm});
            skLineSegment(sketch, "E29.5.0.1", {"start": v(-140.73, 70.6) * mm, "end": v(-140.61, 65.6) * mm});
            skLineSegment(sketch, "E29.5.0.2", {"start": v(-149.39, 70.4) * mm, "end": v(-145.11, 73) * mm});
            skLineSegment(sketch, "E29.5.0.3", {"start": v(-149.27, 65.4) * mm, "end": v(-149.39, 70.4) * mm});
            skLineSegment(sketch, "E29.5.0.4", {"start": v(-144.89, 63) * mm, "end": v(-149.27, 65.4) * mm});
            skLineSegment(sketch, "E29.5.0.5", {"start": v(-140.61, 65.6) * mm, "end": v(-144.89, 63) * mm});
            skLineSegment(sketch, "E29.5.1.0", {"start": v(-145, 53) * mm, "end": v(-140.61, 50.6) * mm});
            skLineSegment(sketch, "E29.5.1.1", {"start": v(-140.61, 50.6) * mm, "end": v(-140.5, 45.6) * mm});
            skLineSegment(sketch, "E29.5.1.2", {"start": v(-149.27, 50.4) * mm, "end": v(-145, 53) * mm});
            skLineSegment(sketch, "E29.5.1.3", {"start": v(-149.16, 45.4) * mm, "end": v(-149.27, 50.4) * mm});
            skLineSegment(sketch, "E29.5.1.4", {"start": v(-144.77, 43) * mm, "end": v(-149.16, 45.4) * mm});
            skLineSegment(sketch, "E29.5.1.5", {"start": v(-140.5, 45.6) * mm, "end": v(-144.77, 43) * mm});
            skLineSegment(sketch, "E29.5.2.0", {"start": v(-144.89, 33) * mm, "end": v(-140.5, 30.6) * mm});
            skLineSegment(sketch, "E29.5.2.1", {"start": v(-140.5, 30.6) * mm, "end": v(-140.38, 25.6) * mm});
            skLineSegment(sketch, "E29.5.2.2", {"start": v(-149.16, 30.4) * mm, "end": v(-144.89, 33) * mm});
            skLineSegment(sketch, "E29.5.2.3", {"start": v(-149.04, 25.4) * mm, "end": v(-149.16, 30.4) * mm});
            skLineSegment(sketch, "E29.5.2.4", {"start": v(-144.66, 23) * mm, "end": v(-149.04, 25.4) * mm});
            skLineSegment(sketch, "E29.5.2.5", {"start": v(-140.38, 25.6) * mm, "end": v(-144.66, 23) * mm});
            skLineSegment(sketch, "E29.5.3.0", {"start": v(-144.77, 13) * mm, "end": v(-140.38, 10.6) * mm});
            skLineSegment(sketch, "E29.5.3.1", {"start": v(-140.38, 10.6) * mm, "end": v(-140.27, 5.6) * mm});
            skLineSegment(sketch, "E29.5.3.2", {"start": v(-149.04, 10.4) * mm, "end": v(-144.77, 13) * mm});
            skLineSegment(sketch, "E29.5.3.3", {"start": v(-148.93, 5.41) * mm, "end": v(-149.04, 10.4) * mm});
            skLineSegment(sketch, "E29.5.3.4", {"start": v(-144.54, 3) * mm, "end": v(-148.93, 5.41) * mm});
            skLineSegment(sketch, "E29.5.3.5", {"start": v(-140.27, 5.6) * mm, "end": v(-144.54, 3) * mm});
            skLineSegment(sketch, "E29.5.4.0", {"start": v(-144.66, -7) * mm, "end": v(-140.27, -9.4) * mm});
            skLineSegment(sketch, "E29.5.4.1", {"start": v(-140.27, -9.4) * mm, "end": v(-140.16, -14.4) * mm});
            skLineSegment(sketch, "E29.5.4.2", {"start": v(-148.93, -9.59) * mm, "end": v(-144.66, -7) * mm});
            skLineSegment(sketch, "E29.5.4.3", {"start": v(-148.81, -14.59) * mm, "end": v(-148.93, -9.59) * mm});
            skLineSegment(sketch, "E29.5.4.4", {"start": v(-144.43, -16.99) * mm, "end": v(-148.81, -14.59) * mm});
            skLineSegment(sketch, "E29.5.4.5", {"start": v(-140.16, -14.4) * mm, "end": v(-144.43, -16.99) * mm});
            skLineSegment(sketch, "E29.5.5.0", {"start": v(-144.54, -27) * mm, "end": v(-140.16, -29.4) * mm});
            skLineSegment(sketch, "E29.5.5.1", {"start": v(-140.16, -29.4) * mm, "end": v(-140.04, -34.39) * mm});
            skLineSegment(sketch, "E29.5.5.2", {"start": v(-148.81, -29.59) * mm, "end": v(-144.54, -27) * mm});
            skLineSegment(sketch, "E29.5.5.3", {"start": v(-148.7, -34.59) * mm, "end": v(-148.81, -29.59) * mm});
            skLineSegment(sketch, "E29.5.5.4", {"start": v(-144.31, -36.99) * mm, "end": v(-148.7, -34.59) * mm});
            skLineSegment(sketch, "E29.5.5.5", {"start": v(-140.04, -34.39) * mm, "end": v(-144.31, -36.99) * mm});
            skLineSegment(sketch, "E29.5.6.0", {"start": v(-144.43, -46.99) * mm, "end": v(-140.04, -49.39) * mm});
            skLineSegment(sketch, "E29.5.6.1", {"start": v(-140.04, -49.39) * mm, "end": v(-139.93, -54.39) * mm});
            skLineSegment(sketch, "E29.5.6.2", {"start": v(-148.7, -49.59) * mm, "end": v(-144.43, -46.99) * mm});
            skLineSegment(sketch, "E29.5.6.3", {"start": v(-148.59, -54.59) * mm, "end": v(-148.7, -49.59) * mm});
            skLineSegment(sketch, "E29.5.6.4", {"start": v(-144.2, -56.99) * mm, "end": v(-148.59, -54.59) * mm});
            skLineSegment(sketch, "E29.5.6.5", {"start": v(-139.93, -54.39) * mm, "end": v(-144.2, -56.99) * mm});
            skLineSegment(sketch, "E29.6.0.0", {"start": v(-131.11, 73) * mm, "end": v(-126.73, 70.6) * mm});
            skLineSegment(sketch, "E29.6.0.1", {"start": v(-126.73, 70.6) * mm, "end": v(-126.61, 65.6) * mm});
            skLineSegment(sketch, "E29.6.0.2", {"start": v(-135.39, 70.4) * mm, "end": v(-131.11, 73) * mm});
            skLineSegment(sketch, "E29.6.0.3", {"start": v(-135.27, 65.4) * mm, "end": v(-135.39, 70.4) * mm});
            skLineSegment(sketch, "E29.6.0.4", {"start": v(-130.89, 63) * mm, "end": v(-135.27, 65.4) * mm});
            skLineSegment(sketch, "E29.6.0.5", {"start": v(-126.61, 65.6) * mm, "end": v(-130.89, 63) * mm});
            skLineSegment(sketch, "E29.6.1.0", {"start": v(-131, 53) * mm, "end": v(-126.61, 50.6) * mm});
            skLineSegment(sketch, "E29.6.1.1", {"start": v(-126.61, 50.6) * mm, "end": v(-126.5, 45.6) * mm});
            skLineSegment(sketch, "E29.6.1.2", {"start": v(-135.27, 50.4) * mm, "end": v(-131, 53) * mm});
            skLineSegment(sketch, "E29.6.1.3", {"start": v(-135.16, 45.4) * mm, "end": v(-135.27, 50.4) * mm});
            skLineSegment(sketch, "E29.6.1.4", {"start": v(-130.77, 43) * mm, "end": v(-135.16, 45.4) * mm});
            skLineSegment(sketch, "E29.6.1.5", {"start": v(-126.5, 45.6) * mm, "end": v(-130.77, 43) * mm});
            skLineSegment(sketch, "E29.6.2.0", {"start": v(-130.89, 33) * mm, "end": v(-126.5, 30.6) * mm});
            skLineSegment(sketch, "E29.6.2.1", {"start": v(-126.5, 30.6) * mm, "end": v(-126.38, 25.6) * mm});
            skLineSegment(sketch, "E29.6.2.2", {"start": v(-135.16, 30.4) * mm, "end": v(-130.89, 33) * mm});
            skLineSegment(sketch, "E29.6.2.3", {"start": v(-135.04, 25.4) * mm, "end": v(-135.16, 30.4) * mm});
            skLineSegment(sketch, "E29.6.2.4", {"start": v(-130.66, 23) * mm, "end": v(-135.04, 25.4) * mm});
            skLineSegment(sketch, "E29.6.2.5", {"start": v(-126.38, 25.6) * mm, "end": v(-130.66, 23) * mm});
            skLineSegment(sketch, "E29.6.3.0", {"start": v(-130.77, 13) * mm, "end": v(-126.38, 10.6) * mm});
            skLineSegment(sketch, "E29.6.3.1", {"start": v(-126.38, 10.6) * mm, "end": v(-126.27, 5.6) * mm});
            skLineSegment(sketch, "E29.6.3.2", {"start": v(-135.04, 10.4) * mm, "end": v(-130.77, 13) * mm});
            skLineSegment(sketch, "E29.6.3.3", {"start": v(-134.93, 5.41) * mm, "end": v(-135.04, 10.4) * mm});
            skLineSegment(sketch, "E29.6.3.4", {"start": v(-130.54, 3.01) * mm, "end": v(-134.93, 5.41) * mm});
            skLineSegment(sketch, "E29.6.3.5", {"start": v(-126.27, 5.6) * mm, "end": v(-130.54, 3.01) * mm});
            skLineSegment(sketch, "E29.6.4.0", {"start": v(-130.66, -7) * mm, "end": v(-126.27, -9.4) * mm});
            skLineSegment(sketch, "E29.6.4.1", {"start": v(-126.27, -9.4) * mm, "end": v(-126.16, -14.39) * mm});
            skLineSegment(sketch, "E29.6.4.2", {"start": v(-134.93, -9.59) * mm, "end": v(-130.66, -7) * mm});
            skLineSegment(sketch, "E29.6.4.3", {"start": v(-134.81, -14.59) * mm, "end": v(-134.93, -9.59) * mm});
            skLineSegment(sketch, "E29.6.4.4", {"start": v(-130.43, -16.99) * mm, "end": v(-134.81, -14.59) * mm});
            skLineSegment(sketch, "E29.6.4.5", {"start": v(-126.16, -14.39) * mm, "end": v(-130.43, -16.99) * mm});
            skLineSegment(sketch, "E29.6.5.0", {"start": v(-130.54, -26.99) * mm, "end": v(-126.16, -29.39) * mm});
            skLineSegment(sketch, "E29.6.5.1", {"start": v(-126.16, -29.39) * mm, "end": v(-126.04, -34.39) * mm});
            skLineSegment(sketch, "E29.6.5.2", {"start": v(-134.81, -29.59) * mm, "end": v(-130.54, -26.99) * mm});
            skLineSegment(sketch, "E29.6.5.3", {"start": v(-134.7, -34.59) * mm, "end": v(-134.81, -29.59) * mm});
            skLineSegment(sketch, "E29.6.5.4", {"start": v(-130.31, -36.99) * mm, "end": v(-134.7, -34.59) * mm});
            skLineSegment(sketch, "E29.6.5.5", {"start": v(-126.04, -34.39) * mm, "end": v(-130.31, -36.99) * mm});
            skLineSegment(sketch, "E29.6.6.0", {"start": v(-130.43, -46.99) * mm, "end": v(-126.04, -49.39) * mm});
            skLineSegment(sketch, "E29.6.6.1", {"start": v(-126.04, -49.39) * mm, "end": v(-125.93, -54.39) * mm});
            skLineSegment(sketch, "E29.6.6.2", {"start": v(-134.7, -49.59) * mm, "end": v(-130.43, -46.99) * mm});
            skLineSegment(sketch, "E29.6.6.3", {"start": v(-134.59, -54.59) * mm, "end": v(-134.7, -49.59) * mm});
            skLineSegment(sketch, "E29.6.6.4", {"start": v(-130.2, -56.99) * mm, "end": v(-134.59, -54.59) * mm});
            skLineSegment(sketch, "E29.6.6.5", {"start": v(-125.93, -54.39) * mm, "end": v(-130.2, -56.99) * mm});
            skLineSegment(sketch, "E29.7.0.0", {"start": v(-117.11, 73) * mm, "end": v(-112.73, 70.6) * mm});
            skLineSegment(sketch, "E29.7.0.1", {"start": v(-112.73, 70.6) * mm, "end": v(-112.61, 65.6) * mm});
            skLineSegment(sketch, "E29.7.0.2", {"start": v(-121.39, 70.4) * mm, "end": v(-117.11, 73) * mm});
            skLineSegment(sketch, "E29.7.0.3", {"start": v(-121.27, 65.4) * mm, "end": v(-121.39, 70.4) * mm});
            skLineSegment(sketch, "E29.7.0.4", {"start": v(-116.89, 63) * mm, "end": v(-121.27, 65.4) * mm});
            skLineSegment(sketch, "E29.7.0.5", {"start": v(-112.61, 65.6) * mm, "end": v(-116.89, 63) * mm});
            skLineSegment(sketch, "E29.7.1.0", {"start": v(-117, 53) * mm, "end": v(-112.61, 50.6) * mm});
            skLineSegment(sketch, "E29.7.1.1", {"start": v(-112.61, 50.6) * mm, "end": v(-112.5, 45.6) * mm});
            skLineSegment(sketch, "E29.7.1.2", {"start": v(-121.27, 50.4) * mm, "end": v(-117, 53) * mm});
            skLineSegment(sketch, "E29.7.1.3", {"start": v(-121.16, 45.4) * mm, "end": v(-121.27, 50.4) * mm});
            skLineSegment(sketch, "E29.7.1.4", {"start": v(-116.77, 43) * mm, "end": v(-121.16, 45.4) * mm});
            skLineSegment(sketch, "E29.7.1.5", {"start": v(-112.5, 45.6) * mm, "end": v(-116.77, 43) * mm});
            skLineSegment(sketch, "E29.7.2.0", {"start": v(-116.89, 33) * mm, "end": v(-112.5, 30.6) * mm});
            skLineSegment(sketch, "E29.7.2.1", {"start": v(-112.5, 30.6) * mm, "end": v(-112.38, 25.6) * mm});
            skLineSegment(sketch, "E29.7.2.2", {"start": v(-121.16, 30.4) * mm, "end": v(-116.89, 33) * mm});
            skLineSegment(sketch, "E29.7.2.3", {"start": v(-121.04, 25.41) * mm, "end": v(-121.16, 30.4) * mm});
            skLineSegment(sketch, "E29.7.2.4", {"start": v(-116.66, 23.01) * mm, "end": v(-121.04, 25.41) * mm});
            skLineSegment(sketch, "E29.7.2.5", {"start": v(-112.38, 25.6) * mm, "end": v(-116.66, 23.01) * mm});
            skLineSegment(sketch, "E29.7.3.0", {"start": v(-116.77, 13) * mm, "end": v(-112.38, 10.6) * mm});
            skLineSegment(sketch, "E29.7.3.1", {"start": v(-112.38, 10.6) * mm, "end": v(-112.27, 5.61) * mm});
            skLineSegment(sketch, "E29.7.3.2", {"start": v(-121.04, 10.41) * mm, "end": v(-116.77, 13) * mm});
            skLineSegment(sketch, "E29.7.3.3", {"start": v(-120.93, 5.41) * mm, "end": v(-121.04, 10.41) * mm});
            skLineSegment(sketch, "E29.7.3.4", {"start": v(-116.54, 3.01) * mm, "end": v(-120.93, 5.41) * mm});
            skLineSegment(sketch, "E29.7.3.5", {"start": v(-112.27, 5.61) * mm, "end": v(-116.54, 3.01) * mm});
            skLineSegment(sketch, "E29.7.4.0", {"start": v(-116.66, -6.99) * mm, "end": v(-112.27, -9.39) * mm});
            skLineSegment(sketch, "E29.7.4.1", {"start": v(-112.27, -9.39) * mm, "end": v(-112.16, -14.39) * mm});
            skLineSegment(sketch, "E29.7.4.2", {"start": v(-120.93, -9.59) * mm, "end": v(-116.66, -6.99) * mm});
            skLineSegment(sketch, "E29.7.4.3", {"start": v(-120.81, -14.59) * mm, "end": v(-120.93, -9.59) * mm});
            skLineSegment(sketch, "E29.7.4.4", {"start": v(-116.43, -16.99) * mm, "end": v(-120.81, -14.59) * mm});
            skLineSegment(sketch, "E29.7.4.5", {"start": v(-112.16, -14.39) * mm, "end": v(-116.43, -16.99) * mm});
            skLineSegment(sketch, "E29.7.5.0", {"start": v(-116.54, -26.99) * mm, "end": v(-112.16, -29.39) * mm});
            skLineSegment(sketch, "E29.7.5.1", {"start": v(-112.16, -29.39) * mm, "end": v(-112.04, -34.39) * mm});
            skLineSegment(sketch, "E29.7.5.2", {"start": v(-120.81, -29.59) * mm, "end": v(-116.54, -26.99) * mm});
            skLineSegment(sketch, "E29.7.5.3", {"start": v(-120.7, -34.59) * mm, "end": v(-120.81, -29.59) * mm});
            skLineSegment(sketch, "E29.7.5.4", {"start": v(-116.31, -36.99) * mm, "end": v(-120.7, -34.59) * mm});
            skLineSegment(sketch, "E29.7.5.5", {"start": v(-112.04, -34.39) * mm, "end": v(-116.31, -36.99) * mm});
            skLineSegment(sketch, "E29.7.6.0", {"start": v(-116.43, -46.99) * mm, "end": v(-112.04, -49.39) * mm});
            skLineSegment(sketch, "E29.7.6.1", {"start": v(-112.04, -49.39) * mm, "end": v(-111.93, -54.39) * mm});
            skLineSegment(sketch, "E29.7.6.2", {"start": v(-120.7, -49.59) * mm, "end": v(-116.43, -46.99) * mm});
            skLineSegment(sketch, "E29.7.6.3", {"start": v(-120.59, -54.58) * mm, "end": v(-120.7, -49.59) * mm});
            skLineSegment(sketch, "E29.7.6.4", {"start": v(-116.2, -56.98) * mm, "end": v(-120.59, -54.58) * mm});
            skLineSegment(sketch, "E29.7.6.5", {"start": v(-111.93, -54.39) * mm, "end": v(-116.2, -56.98) * mm});
            skLineSegment(sketch, "E29.8.0.0", {"start": v(-103.11, 73) * mm, "end": v(-98.73, 70.6) * mm});
            skLineSegment(sketch, "E29.8.0.1", {"start": v(-98.73, 70.6) * mm, "end": v(-98.61, 65.6) * mm});
            skLineSegment(sketch, "E29.8.0.2", {"start": v(-107.39, 70.4) * mm, "end": v(-103.11, 73) * mm});
            skLineSegment(sketch, "E29.8.0.3", {"start": v(-107.27, 65.4) * mm, "end": v(-107.39, 70.4) * mm});
            skLineSegment(sketch, "E29.8.0.4", {"start": v(-102.89, 63) * mm, "end": v(-107.27, 65.4) * mm});
            skLineSegment(sketch, "E29.8.0.5", {"start": v(-98.61, 65.6) * mm, "end": v(-102.89, 63) * mm});
            skLineSegment(sketch, "E29.8.1.0", {"start": v(-103, 53) * mm, "end": v(-98.61, 50.6) * mm});
            skLineSegment(sketch, "E29.8.1.1", {"start": v(-98.61, 50.6) * mm, "end": v(-98.5, 45.6) * mm});
            skLineSegment(sketch, "E29.8.1.2", {"start": v(-107.27, 50.4) * mm, "end": v(-103, 53) * mm});
            skLineSegment(sketch, "E29.8.1.3", {"start": v(-107.16, 45.41) * mm, "end": v(-107.27, 50.4) * mm});
            skLineSegment(sketch, "E29.8.1.4", {"start": v(-102.77, 43) * mm, "end": v(-107.16, 45.41) * mm});
            skLineSegment(sketch, "E29.8.1.5", {"start": v(-98.5, 45.6) * mm, "end": v(-102.77, 43) * mm});
            skLineSegment(sketch, "E29.8.2.0", {"start": v(-102.89, 33) * mm, "end": v(-98.5, 30.6) * mm});
            skLineSegment(sketch, "E29.8.2.1", {"start": v(-98.5, 30.6) * mm, "end": v(-98.38, 25.6) * mm});
            skLineSegment(sketch, "E29.8.2.2", {"start": v(-107.16, 30.41) * mm, "end": v(-102.89, 33) * mm});
            skLineSegment(sketch, "E29.8.2.3", {"start": v(-107.04, 25.41) * mm, "end": v(-107.16, 30.41) * mm});
            skLineSegment(sketch, "E29.8.2.4", {"start": v(-102.66, 23.01) * mm, "end": v(-107.04, 25.41) * mm});
            skLineSegment(sketch, "E29.8.2.5", {"start": v(-98.38, 25.6) * mm, "end": v(-102.66, 23.01) * mm});
            skLineSegment(sketch, "E29.8.3.0", {"start": v(-102.77, 13) * mm, "end": v(-98.38, 10.6) * mm});
            skLineSegment(sketch, "E29.8.3.1", {"start": v(-98.38, 10.6) * mm, "end": v(-98.27, 5.61) * mm});
            skLineSegment(sketch, "E29.8.3.2", {"start": v(-107.04, 10.41) * mm, "end": v(-102.77, 13) * mm});
            skLineSegment(sketch, "E29.8.3.3", {"start": v(-106.93, 5.41) * mm, "end": v(-107.04, 10.41) * mm});
            skLineSegment(sketch, "E29.8.3.4", {"start": v(-102.54, 3.01) * mm, "end": v(-106.93, 5.41) * mm});
            skLineSegment(sketch, "E29.8.3.5", {"start": v(-98.27, 5.61) * mm, "end": v(-102.54, 3.01) * mm});
            skLineSegment(sketch, "E29.8.4.0", {"start": v(-102.66, -6.99) * mm, "end": v(-98.27, -9.39) * mm});
            skLineSegment(sketch, "E29.8.4.1", {"start": v(-98.27, -9.39) * mm, "end": v(-98.16, -14.39) * mm});
            skLineSegment(sketch, "E29.8.4.2", {"start": v(-106.93, -9.59) * mm, "end": v(-102.66, -6.99) * mm});
            skLineSegment(sketch, "E29.8.4.3", {"start": v(-106.81, -14.59) * mm, "end": v(-106.93, -9.59) * mm});
            skLineSegment(sketch, "E29.8.4.4", {"start": v(-102.43, -16.99) * mm, "end": v(-106.81, -14.59) * mm});
            skLineSegment(sketch, "E29.8.4.5", {"start": v(-98.16, -14.39) * mm, "end": v(-102.43, -16.99) * mm});
            skLineSegment(sketch, "E29.8.5.0", {"start": v(-102.54, -26.99) * mm, "end": v(-98.16, -29.39) * mm});
            skLineSegment(sketch, "E29.8.5.1", {"start": v(-98.16, -29.39) * mm, "end": v(-98.04, -34.39) * mm});
            skLineSegment(sketch, "E29.8.5.2", {"start": v(-106.81, -29.59) * mm, "end": v(-102.54, -26.99) * mm});
            skLineSegment(sketch, "E29.8.5.3", {"start": v(-106.7, -34.58) * mm, "end": v(-106.81, -29.59) * mm});
            skLineSegment(sketch, "E29.8.5.4", {"start": v(-102.31, -36.98) * mm, "end": v(-106.7, -34.58) * mm});
            skLineSegment(sketch, "E29.8.5.5", {"start": v(-98.04, -34.39) * mm, "end": v(-102.31, -36.98) * mm});
            skLineSegment(sketch, "E29.8.6.0", {"start": v(-102.43, -46.99) * mm, "end": v(-98.04, -49.39) * mm});
            skLineSegment(sketch, "E29.8.6.1", {"start": v(-98.04, -49.39) * mm, "end": v(-97.93, -54.39) * mm});
            skLineSegment(sketch, "E29.8.6.2", {"start": v(-106.7, -49.58) * mm, "end": v(-102.43, -46.99) * mm});
            skLineSegment(sketch, "E29.8.6.3", {"start": v(-106.59, -54.58) * mm, "end": v(-106.7, -49.58) * mm});
            skLineSegment(sketch, "E29.8.6.4", {"start": v(-102.2, -56.98) * mm, "end": v(-106.59, -54.58) * mm});
            skLineSegment(sketch, "E29.8.6.5", {"start": v(-97.93, -54.39) * mm, "end": v(-102.2, -56.98) * mm});
            skLineSegment(sketch, "E29.9.0.0", {"start": v(-89.11, 73) * mm, "end": v(-84.73, 70.6) * mm});
            skLineSegment(sketch, "E29.9.0.1", {"start": v(-84.73, 70.6) * mm, "end": v(-84.61, 65.6) * mm});
            skLineSegment(sketch, "E29.9.0.2", {"start": v(-93.39, 70.4) * mm, "end": v(-89.11, 73) * mm});
            skLineSegment(sketch, "E29.9.0.3", {"start": v(-93.27, 65.4) * mm, "end": v(-93.39, 70.4) * mm});
            skLineSegment(sketch, "E29.9.0.4", {"start": v(-88.89, 63) * mm, "end": v(-93.27, 65.4) * mm});
            skLineSegment(sketch, "E29.9.0.5", {"start": v(-84.61, 65.6) * mm, "end": v(-88.89, 63) * mm});
            skLineSegment(sketch, "E29.9.1.0", {"start": v(-89, 53) * mm, "end": v(-84.61, 50.6) * mm});
            skLineSegment(sketch, "E29.9.1.1", {"start": v(-84.61, 50.6) * mm, "end": v(-84.5, 45.6) * mm});
            skLineSegment(sketch, "E29.9.1.2", {"start": v(-93.27, 50.4) * mm, "end": v(-89, 53) * mm});
            skLineSegment(sketch, "E29.9.1.3", {"start": v(-93.16, 45.41) * mm, "end": v(-93.27, 50.4) * mm});
            skLineSegment(sketch, "E29.9.1.4", {"start": v(-88.77, 43.01) * mm, "end": v(-93.16, 45.41) * mm});
            skLineSegment(sketch, "E29.9.1.5", {"start": v(-84.5, 45.6) * mm, "end": v(-88.77, 43.01) * mm});
            skLineSegment(sketch, "E29.9.2.0", {"start": v(-88.89, 33) * mm, "end": v(-84.5, 30.6) * mm});
            skLineSegment(sketch, "E29.9.2.1", {"start": v(-84.5, 30.6) * mm, "end": v(-84.38, 25.61) * mm});
            skLineSegment(sketch, "E29.9.2.2", {"start": v(-93.16, 30.41) * mm, "end": v(-88.89, 33) * mm});
            skLineSegment(sketch, "E29.9.2.3", {"start": v(-93.04, 25.41) * mm, "end": v(-93.16, 30.41) * mm});
            skLineSegment(sketch, "E29.9.2.4", {"start": v(-88.66, 23.01) * mm, "end": v(-93.04, 25.41) * mm});
            skLineSegment(sketch, "E29.9.2.5", {"start": v(-84.38, 25.61) * mm, "end": v(-88.66, 23.01) * mm});
            skLineSegment(sketch, "E29.9.3.0", {"start": v(-88.77, 13.01) * mm, "end": v(-84.38, 10.61) * mm});
            skLineSegment(sketch, "E29.9.3.1", {"start": v(-84.38, 10.61) * mm, "end": v(-84.27, 5.61) * mm});
            skLineSegment(sketch, "E29.9.3.2", {"start": v(-93.04, 10.41) * mm, "end": v(-88.77, 13.01) * mm});
            skLineSegment(sketch, "E29.9.3.3", {"start": v(-92.93, 5.41) * mm, "end": v(-93.04, 10.41) * mm});
            skLineSegment(sketch, "E29.9.3.4", {"start": v(-88.54, 3.01) * mm, "end": v(-92.93, 5.41) * mm});
            skLineSegment(sketch, "E29.9.3.5", {"start": v(-84.27, 5.61) * mm, "end": v(-88.54, 3.01) * mm});
            skLineSegment(sketch, "E29.9.4.0", {"start": v(-88.66, -6.99) * mm, "end": v(-84.27, -9.39) * mm});
            skLineSegment(sketch, "E29.9.4.1", {"start": v(-84.27, -9.39) * mm, "end": v(-84.16, -14.39) * mm});
            skLineSegment(sketch, "E29.9.4.2", {"start": v(-92.93, -9.59) * mm, "end": v(-88.66, -6.99) * mm});
            skLineSegment(sketch, "E29.9.4.3", {"start": v(-92.81, -14.58) * mm, "end": v(-92.93, -9.59) * mm});
            skLineSegment(sketch, "E29.9.4.4", {"start": v(-88.43, -16.99) * mm, "end": v(-92.81, -14.58) * mm});
            skLineSegment(sketch, "E29.9.4.5", {"start": v(-84.16, -14.39) * mm, "end": v(-88.43, -16.99) * mm});
            skLineSegment(sketch, "E29.9.5.0", {"start": v(-88.54, -26.99) * mm, "end": v(-84.16, -29.39) * mm});
            skLineSegment(sketch, "E29.9.5.1", {"start": v(-84.16, -29.39) * mm, "end": v(-84.04, -34.39) * mm});
            skLineSegment(sketch, "E29.9.5.2", {"start": v(-92.81, -29.58) * mm, "end": v(-88.54, -26.99) * mm});
            skLineSegment(sketch, "E29.9.5.3", {"start": v(-92.7, -34.58) * mm, "end": v(-92.81, -29.58) * mm});
            skLineSegment(sketch, "E29.9.5.4", {"start": v(-88.31, -36.98) * mm, "end": v(-92.7, -34.58) * mm});
            skLineSegment(sketch, "E29.9.5.5", {"start": v(-84.04, -34.39) * mm, "end": v(-88.31, -36.98) * mm});
            skLineSegment(sketch, "E29.9.6.0", {"start": v(-88.43, -46.99) * mm, "end": v(-84.04, -49.39) * mm});
            skLineSegment(sketch, "E29.9.6.1", {"start": v(-84.04, -49.39) * mm, "end": v(-83.93, -54.38) * mm});
            skLineSegment(sketch, "E29.9.6.2", {"start": v(-92.7, -49.58) * mm, "end": v(-88.43, -46.99) * mm});
            skLineSegment(sketch, "E29.9.6.3", {"start": v(-92.59, -54.58) * mm, "end": v(-92.7, -49.58) * mm});
            skLineSegment(sketch, "E29.9.6.4", {"start": v(-88.2, -56.98) * mm, "end": v(-92.59, -54.58) * mm});
            skLineSegment(sketch, "E29.9.6.5", {"start": v(-83.93, -54.38) * mm, "end": v(-88.2, -56.98) * mm});
            skLineSegment(sketch, "E29.10.0.0", {"start": v(-75.11, 73) * mm, "end": v(-70.73, 70.6) * mm});
            skLineSegment(sketch, "E29.10.0.1", {"start": v(-70.73, 70.6) * mm, "end": v(-70.61, 65.6) * mm});
            skLineSegment(sketch, "E29.10.0.2", {"start": v(-79.39, 70.4) * mm, "end": v(-75.11, 73) * mm});
            skLineSegment(sketch, "E29.10.0.3", {"start": v(-79.27, 65.41) * mm, "end": v(-79.39, 70.4) * mm});
            skLineSegment(sketch, "E29.10.0.4", {"start": v(-74.89, 63.01) * mm, "end": v(-79.27, 65.41) * mm});
            skLineSegment(sketch, "E29.10.0.5", {"start": v(-70.61, 65.6) * mm, "end": v(-74.89, 63.01) * mm});
            skLineSegment(sketch, "E29.10.1.0", {"start": v(-75, 53) * mm, "end": v(-70.61, 50.6) * mm});
            skLineSegment(sketch, "E29.10.1.1", {"start": v(-70.61, 50.6) * mm, "end": v(-70.5, 45.61) * mm});
            skLineSegment(sketch, "E29.10.1.2", {"start": v(-79.27, 50.41) * mm, "end": v(-75, 53) * mm});
            skLineSegment(sketch, "E29.10.1.3", {"start": v(-79.16, 45.41) * mm, "end": v(-79.27, 50.41) * mm});
            skLineSegment(sketch, "E29.10.1.4", {"start": v(-74.77, 43.01) * mm, "end": v(-79.16, 45.41) * mm});
            skLineSegment(sketch, "E29.10.1.5", {"start": v(-70.5, 45.61) * mm, "end": v(-74.77, 43.01) * mm});
            skLineSegment(sketch, "E29.10.2.0", {"start": v(-74.89, 33.01) * mm, "end": v(-70.5, 30.61) * mm});
            skLineSegment(sketch, "E29.10.2.1", {"start": v(-70.5, 30.61) * mm, "end": v(-70.38, 25.61) * mm});
            skLineSegment(sketch, "E29.10.2.2", {"start": v(-79.16, 30.41) * mm, "end": v(-74.89, 33.01) * mm});
            skLineSegment(sketch, "E29.10.2.3", {"start": v(-79.04, 25.41) * mm, "end": v(-79.16, 30.41) * mm});
            skLineSegment(sketch, "E29.10.2.4", {"start": v(-74.66, 23.01) * mm, "end": v(-79.04, 25.41) * mm});
            skLineSegment(sketch, "E29.10.2.5", {"start": v(-70.38, 25.61) * mm, "end": v(-74.66, 23.01) * mm});
            skLineSegment(sketch, "E29.10.3.0", {"start": v(-74.77, 13.01) * mm, "end": v(-70.38, 10.61) * mm});
            skLineSegment(sketch, "E29.10.3.1", {"start": v(-70.38, 10.61) * mm, "end": v(-70.27, 5.61) * mm});
            skLineSegment(sketch, "E29.10.3.2", {"start": v(-79.04, 10.41) * mm, "end": v(-74.77, 13.01) * mm});
            skLineSegment(sketch, "E29.10.3.3", {"start": v(-78.93, 5.41) * mm, "end": v(-79.04, 10.41) * mm});
            skLineSegment(sketch, "E29.10.3.4", {"start": v(-74.54, 3.01) * mm, "end": v(-78.93, 5.41) * mm});
            skLineSegment(sketch, "E29.10.3.5", {"start": v(-70.27, 5.61) * mm, "end": v(-74.54, 3.01) * mm});
            skLineSegment(sketch, "E29.10.4.0", {"start": v(-74.66, -6.99) * mm, "end": v(-70.27, -9.39) * mm});
            skLineSegment(sketch, "E29.10.4.1", {"start": v(-70.27, -9.39) * mm, "end": v(-70.16, -14.39) * mm});
            skLineSegment(sketch, "E29.10.4.2", {"start": v(-78.93, -9.59) * mm, "end": v(-74.66, -6.99) * mm});
            skLineSegment(sketch, "E29.10.4.3", {"start": v(-78.81, -14.58) * mm, "end": v(-78.93, -9.59) * mm});
            skLineSegment(sketch, "E29.10.4.4", {"start": v(-74.43, -16.98) * mm, "end": v(-78.81, -14.58) * mm});
            skLineSegment(sketch, "E29.10.4.5", {"start": v(-70.16, -14.39) * mm, "end": v(-74.43, -16.98) * mm});
            skLineSegment(sketch, "E29.10.5.0", {"start": v(-74.54, -26.99) * mm, "end": v(-70.16, -29.39) * mm});
            skLineSegment(sketch, "E29.10.5.1", {"start": v(-70.16, -29.39) * mm, "end": v(-70.04, -34.38) * mm});
            skLineSegment(sketch, "E29.10.5.2", {"start": v(-78.81, -29.58) * mm, "end": v(-74.54, -26.99) * mm});
            skLineSegment(sketch, "E29.10.5.3", {"start": v(-78.7, -34.58) * mm, "end": v(-78.81, -29.58) * mm});
            skLineSegment(sketch, "E29.10.5.4", {"start": v(-74.31, -36.98) * mm, "end": v(-78.7, -34.58) * mm});
            skLineSegment(sketch, "E29.10.5.5", {"start": v(-70.04, -34.38) * mm, "end": v(-74.31, -36.98) * mm});
            skLineSegment(sketch, "E29.10.6.0", {"start": v(-74.43, -46.98) * mm, "end": v(-70.04, -49.38) * mm});
            skLineSegment(sketch, "E29.10.6.1", {"start": v(-70.04, -49.38) * mm, "end": v(-69.93, -54.38) * mm});
            skLineSegment(sketch, "E29.10.6.2", {"start": v(-78.7, -49.58) * mm, "end": v(-74.43, -46.98) * mm});
            skLineSegment(sketch, "E29.10.6.3", {"start": v(-78.59, -54.58) * mm, "end": v(-78.7, -49.58) * mm});
            skLineSegment(sketch, "E29.10.6.4", {"start": v(-74.2, -56.98) * mm, "end": v(-78.59, -54.58) * mm});
            skLineSegment(sketch, "E29.10.6.5", {"start": v(-69.93, -54.38) * mm, "end": v(-74.2, -56.98) * mm});
            skLineSegment(sketch, "E29.11.0.0", {"start": v(-61.11, 73) * mm, "end": v(-56.73, 70.6) * mm});
            skLineSegment(sketch, "E29.11.0.1", {"start": v(-56.73, 70.6) * mm, "end": v(-56.61, 65.6) * mm});
            skLineSegment(sketch, "E29.11.0.2", {"start": v(-65.39, 70.41) * mm, "end": v(-61.11, 73) * mm});
            skLineSegment(sketch, "E29.11.0.3", {"start": v(-65.27, 65.41) * mm, "end": v(-65.39, 70.41) * mm});
            skLineSegment(sketch, "E29.11.0.4", {"start": v(-60.89, 63.01) * mm, "end": v(-65.27, 65.41) * mm});
            skLineSegment(sketch, "E29.11.0.5", {"start": v(-56.61, 65.6) * mm, "end": v(-60.89, 63.01) * mm});
            skLineSegment(sketch, "E29.11.1.0", {"start": v(-61, 53.01) * mm, "end": v(-56.61, 50.6) * mm});
            skLineSegment(sketch, "E29.11.1.1", {"start": v(-56.61, 50.6) * mm, "end": v(-56.5, 45.61) * mm});
            skLineSegment(sketch, "E29.11.1.2", {"start": v(-65.27, 50.41) * mm, "end": v(-61, 53.01) * mm});
            skLineSegment(sketch, "E29.11.1.3", {"start": v(-65.16, 45.41) * mm, "end": v(-65.27, 50.41) * mm});
            skLineSegment(sketch, "E29.11.1.4", {"start": v(-60.77, 43.01) * mm, "end": v(-65.16, 45.41) * mm});
            skLineSegment(sketch, "E29.11.1.5", {"start": v(-56.5, 45.61) * mm, "end": v(-60.77, 43.01) * mm});
            skLineSegment(sketch, "E29.11.2.0", {"start": v(-60.89, 33.01) * mm, "end": v(-56.5, 30.61) * mm});
            skLineSegment(sketch, "E29.11.2.1", {"start": v(-56.5, 30.61) * mm, "end": v(-56.38, 25.61) * mm});
            skLineSegment(sketch, "E29.11.2.2", {"start": v(-65.16, 30.41) * mm, "end": v(-60.89, 33.01) * mm});
            skLineSegment(sketch, "E29.11.2.3", {"start": v(-65.04, 25.41) * mm, "end": v(-65.16, 30.41) * mm});
            skLineSegment(sketch, "E29.11.2.4", {"start": v(-60.66, 23.01) * mm, "end": v(-65.04, 25.41) * mm});
            skLineSegment(sketch, "E29.11.2.5", {"start": v(-56.38, 25.61) * mm, "end": v(-60.66, 23.01) * mm});
            skLineSegment(sketch, "E29.11.3.0", {"start": v(-60.77, 13.01) * mm, "end": v(-56.38, 10.61) * mm});
            skLineSegment(sketch, "E29.11.3.1", {"start": v(-56.38, 10.61) * mm, "end": v(-56.27, 5.61) * mm});
            skLineSegment(sketch, "E29.11.3.2", {"start": v(-65.04, 10.41) * mm, "end": v(-60.77, 13.01) * mm});
            skLineSegment(sketch, "E29.11.3.3", {"start": v(-64.93, 5.42) * mm, "end": v(-65.04, 10.41) * mm});
            skLineSegment(sketch, "E29.11.3.4", {"start": v(-60.54, 3.02) * mm, "end": v(-64.93, 5.42) * mm});
            skLineSegment(sketch, "E29.11.3.5", {"start": v(-56.27, 5.61) * mm, "end": v(-60.54, 3.02) * mm});
            skLineSegment(sketch, "E29.11.4.0", {"start": v(-60.66, -6.99) * mm, "end": v(-56.27, -9.39) * mm});
            skLineSegment(sketch, "E29.11.4.1", {"start": v(-56.27, -9.39) * mm, "end": v(-56.16, -14.39) * mm});
            skLineSegment(sketch, "E29.11.4.2", {"start": v(-64.93, -9.58) * mm, "end": v(-60.66, -6.99) * mm});
            skLineSegment(sketch, "E29.11.4.3", {"start": v(-64.81, -14.58) * mm, "end": v(-64.93, -9.58) * mm});
            skLineSegment(sketch, "E29.11.4.4", {"start": v(-60.43, -16.98) * mm, "end": v(-64.81, -14.58) * mm});
            skLineSegment(sketch, "E29.11.4.5", {"start": v(-56.16, -14.39) * mm, "end": v(-60.43, -16.98) * mm});
            skLineSegment(sketch, "E29.11.5.0", {"start": v(-60.54, -26.98) * mm, "end": v(-56.16, -29.39) * mm});
            skLineSegment(sketch, "E29.11.5.1", {"start": v(-56.16, -29.39) * mm, "end": v(-56.04, -34.38) * mm});
            skLineSegment(sketch, "E29.11.5.2", {"start": v(-64.81, -29.58) * mm, "end": v(-60.54, -26.98) * mm});
            skLineSegment(sketch, "E29.11.5.3", {"start": v(-64.7, -34.58) * mm, "end": v(-64.81, -29.58) * mm});
            skLineSegment(sketch, "E29.11.5.4", {"start": v(-60.31, -36.98) * mm, "end": v(-64.7, -34.58) * mm});
            skLineSegment(sketch, "E29.11.5.5", {"start": v(-56.04, -34.38) * mm, "end": v(-60.31, -36.98) * mm});
            skLineSegment(sketch, "E29.11.6.0", {"start": v(-60.43, -46.98) * mm, "end": v(-56.04, -49.38) * mm});
            skLineSegment(sketch, "E29.11.6.1", {"start": v(-56.04, -49.38) * mm, "end": v(-55.93, -54.38) * mm});
            skLineSegment(sketch, "E29.11.6.2", {"start": v(-64.7, -49.58) * mm, "end": v(-60.43, -46.98) * mm});
            skLineSegment(sketch, "E29.11.6.3", {"start": v(-64.59, -54.58) * mm, "end": v(-64.7, -49.58) * mm});
            skLineSegment(sketch, "E29.11.6.4", {"start": v(-60.2, -56.98) * mm, "end": v(-64.59, -54.58) * mm});
            skLineSegment(sketch, "E29.11.6.5", {"start": v(-55.93, -54.38) * mm, "end": v(-60.2, -56.98) * mm});
            skLineSegment(sketch, "E29.12.0.0", {"start": v(-47.11, 73) * mm, "end": v(-42.73, 70.6) * mm});
            skLineSegment(sketch, "E29.12.0.1", {"start": v(-42.73, 70.6) * mm, "end": v(-42.61, 65.61) * mm});
            skLineSegment(sketch, "E29.12.0.2", {"start": v(-51.39, 70.41) * mm, "end": v(-47.11, 73) * mm});
            skLineSegment(sketch, "E29.12.0.3", {"start": v(-51.27, 65.41) * mm, "end": v(-51.39, 70.41) * mm});
            skLineSegment(sketch, "E29.12.0.4", {"start": v(-46.89, 63.01) * mm, "end": v(-51.27, 65.41) * mm});
            skLineSegment(sketch, "E29.12.0.5", {"start": v(-42.61, 65.61) * mm, "end": v(-46.89, 63.01) * mm});
            skLineSegment(sketch, "E29.12.1.0", {"start": v(-47, 53.01) * mm, "end": v(-42.61, 50.61) * mm});
            skLineSegment(sketch, "E29.12.1.1", {"start": v(-42.61, 50.61) * mm, "end": v(-42.5, 45.61) * mm});
            skLineSegment(sketch, "E29.12.1.2", {"start": v(-51.27, 50.41) * mm, "end": v(-47, 53.01) * mm});
            skLineSegment(sketch, "E29.12.1.3", {"start": v(-51.16, 45.41) * mm, "end": v(-51.27, 50.41) * mm});
            skLineSegment(sketch, "E29.12.1.4", {"start": v(-46.77, 43.01) * mm, "end": v(-51.16, 45.41) * mm});
            skLineSegment(sketch, "E29.12.1.5", {"start": v(-42.5, 45.61) * mm, "end": v(-46.77, 43.01) * mm});
            skLineSegment(sketch, "E29.12.2.0", {"start": v(-46.89, 33.01) * mm, "end": v(-42.5, 30.61) * mm});
            skLineSegment(sketch, "E29.12.2.1", {"start": v(-42.5, 30.61) * mm, "end": v(-42.38, 25.61) * mm});
            skLineSegment(sketch, "E29.12.2.2", {"start": v(-51.16, 30.41) * mm, "end": v(-46.89, 33.01) * mm});
            skLineSegment(sketch, "E29.12.2.3", {"start": v(-51.04, 25.42) * mm, "end": v(-51.16, 30.41) * mm});
            skLineSegment(sketch, "E29.12.2.4", {"start": v(-46.66, 23.01) * mm, "end": v(-51.04, 25.42) * mm});
            skLineSegment(sketch, "E29.12.2.5", {"start": v(-42.38, 25.61) * mm, "end": v(-46.66, 23.01) * mm});
            skLineSegment(sketch, "E29.12.3.0", {"start": v(-46.77, 13.01) * mm, "end": v(-42.38, 10.61) * mm});
            skLineSegment(sketch, "E29.12.3.1", {"start": v(-42.38, 10.61) * mm, "end": v(-42.27, 5.61) * mm});
            skLineSegment(sketch, "E29.12.3.2", {"start": v(-51.04, 10.42) * mm, "end": v(-46.77, 13.01) * mm});
            skLineSegment(sketch, "E29.12.3.3", {"start": v(-50.93, 5.42) * mm, "end": v(-51.04, 10.42) * mm});
            skLineSegment(sketch, "E29.12.3.4", {"start": v(-46.54, 3.02) * mm, "end": v(-50.93, 5.42) * mm});
            skLineSegment(sketch, "E29.12.3.5", {"start": v(-42.27, 5.61) * mm, "end": v(-46.54, 3.02) * mm});
            skLineSegment(sketch, "E29.12.4.0", {"start": v(-46.66, -6.99) * mm, "end": v(-42.27, -9.39) * mm});
            skLineSegment(sketch, "E29.12.4.1", {"start": v(-42.27, -9.39) * mm, "end": v(-42.16, -14.38) * mm});
            skLineSegment(sketch, "E29.12.4.2", {"start": v(-50.93, -9.58) * mm, "end": v(-46.66, -6.99) * mm});
            skLineSegment(sketch, "E29.12.4.3", {"start": v(-50.81, -14.58) * mm, "end": v(-50.93, -9.58) * mm});
            skLineSegment(sketch, "E29.12.4.4", {"start": v(-46.43, -16.98) * mm, "end": v(-50.81, -14.58) * mm});
            skLineSegment(sketch, "E29.12.4.5", {"start": v(-42.16, -14.38) * mm, "end": v(-46.43, -16.98) * mm});
            skLineSegment(sketch, "E29.12.5.0", {"start": v(-46.54, -26.98) * mm, "end": v(-42.16, -29.38) * mm});
            skLineSegment(sketch, "E29.12.5.1", {"start": v(-42.16, -29.38) * mm, "end": v(-42.04, -34.38) * mm});
            skLineSegment(sketch, "E29.12.5.2", {"start": v(-50.81, -29.58) * mm, "end": v(-46.54, -26.98) * mm});
            skLineSegment(sketch, "E29.12.5.3", {"start": v(-50.7, -34.58) * mm, "end": v(-50.81, -29.58) * mm});
            skLineSegment(sketch, "E29.12.5.4", {"start": v(-46.31, -36.98) * mm, "end": v(-50.7, -34.58) * mm});
            skLineSegment(sketch, "E29.12.5.5", {"start": v(-42.04, -34.38) * mm, "end": v(-46.31, -36.98) * mm});
            skLineSegment(sketch, "E29.12.6.0", {"start": v(-46.43, -46.98) * mm, "end": v(-42.04, -49.38) * mm});
            skLineSegment(sketch, "E29.12.6.1", {"start": v(-42.04, -49.38) * mm, "end": v(-41.93, -54.38) * mm});
            skLineSegment(sketch, "E29.12.6.2", {"start": v(-50.7, -49.58) * mm, "end": v(-46.43, -46.98) * mm});
            skLineSegment(sketch, "E29.12.6.3", {"start": v(-50.59, -54.58) * mm, "end": v(-50.7, -49.58) * mm});
            skLineSegment(sketch, "E29.12.6.4", {"start": v(-46.2, -56.98) * mm, "end": v(-50.59, -54.58) * mm});
            skLineSegment(sketch, "E29.12.6.5", {"start": v(-41.93, -54.38) * mm, "end": v(-46.2, -56.98) * mm});
            skLineSegment(sketch, "E29.13.0.0", {"start": v(-33.11, 73.01) * mm, "end": v(-28.73, 70.61) * mm});
            skLineSegment(sketch, "E29.13.0.1", {"start": v(-28.73, 70.61) * mm, "end": v(-28.61, 65.61) * mm});
            skLineSegment(sketch, "E29.13.0.2", {"start": v(-37.39, 70.41) * mm, "end": v(-33.11, 73.01) * mm});
            skLineSegment(sketch, "E29.13.0.3", {"start": v(-37.27, 65.41) * mm, "end": v(-37.39, 70.41) * mm});
            skLineSegment(sketch, "E29.13.0.4", {"start": v(-32.89, 63.01) * mm, "end": v(-37.27, 65.41) * mm});
            skLineSegment(sketch, "E29.13.0.5", {"start": v(-28.61, 65.61) * mm, "end": v(-32.89, 63.01) * mm});
            skLineSegment(sketch, "E29.13.1.0", {"start": v(-33, 53.01) * mm, "end": v(-28.61, 50.61) * mm});
            skLineSegment(sketch, "E29.13.1.1", {"start": v(-28.61, 50.61) * mm, "end": v(-28.5, 45.61) * mm});
            skLineSegment(sketch, "E29.13.1.2", {"start": v(-37.27, 50.41) * mm, "end": v(-33, 53.01) * mm});
            skLineSegment(sketch, "E29.13.1.3", {"start": v(-37.16, 45.41) * mm, "end": v(-37.27, 50.41) * mm});
            skLineSegment(sketch, "E29.13.1.4", {"start": v(-32.77, 43.01) * mm, "end": v(-37.16, 45.41) * mm});
            skLineSegment(sketch, "E29.13.1.5", {"start": v(-28.5, 45.61) * mm, "end": v(-32.77, 43.01) * mm});
            skLineSegment(sketch, "E29.13.2.0", {"start": v(-32.89, 33.01) * mm, "end": v(-28.5, 30.61) * mm});
            skLineSegment(sketch, "E29.13.2.1", {"start": v(-28.5, 30.61) * mm, "end": v(-28.38, 25.61) * mm});
            skLineSegment(sketch, "E29.13.2.2", {"start": v(-37.16, 30.41) * mm, "end": v(-32.89, 33.01) * mm});
            skLineSegment(sketch, "E29.13.2.3", {"start": v(-37.04, 25.42) * mm, "end": v(-37.16, 30.41) * mm});
            skLineSegment(sketch, "E29.13.2.4", {"start": v(-32.66, 23.02) * mm, "end": v(-37.04, 25.42) * mm});
            skLineSegment(sketch, "E29.13.2.5", {"start": v(-28.38, 25.61) * mm, "end": v(-32.66, 23.02) * mm});
            skLineSegment(sketch, "E29.13.3.0", {"start": v(-32.77, 13.01) * mm, "end": v(-28.38, 10.61) * mm});
            skLineSegment(sketch, "E29.13.3.1", {"start": v(-28.38, 10.61) * mm, "end": v(-28.27, 5.62) * mm});
            skLineSegment(sketch, "E29.13.3.2", {"start": v(-37.04, 10.42) * mm, "end": v(-32.77, 13.01) * mm});
            skLineSegment(sketch, "E29.13.3.3", {"start": v(-36.93, 5.42) * mm, "end": v(-37.04, 10.42) * mm});
            skLineSegment(sketch, "E29.13.3.4", {"start": v(-32.54, 3.02) * mm, "end": v(-36.93, 5.42) * mm});
            skLineSegment(sketch, "E29.13.3.5", {"start": v(-28.27, 5.62) * mm, "end": v(-32.54, 3.02) * mm});
            skLineSegment(sketch, "E29.13.4.0", {"start": v(-32.66, -6.98) * mm, "end": v(-28.27, -9.38) * mm});
            skLineSegment(sketch, "E29.13.4.1", {"start": v(-28.27, -9.38) * mm, "end": v(-28.16, -14.38) * mm});
            skLineSegment(sketch, "E29.13.4.2", {"start": v(-36.93, -9.58) * mm, "end": v(-32.66, -6.98) * mm});
            skLineSegment(sketch, "E29.13.4.3", {"start": v(-36.81, -14.58) * mm, "end": v(-36.93, -9.58) * mm});
            skLineSegment(sketch, "E29.13.4.4", {"start": v(-32.43, -16.98) * mm, "end": v(-36.81, -14.58) * mm});
            skLineSegment(sketch, "E29.13.4.5", {"start": v(-28.16, -14.38) * mm, "end": v(-32.43, -16.98) * mm});
            skLineSegment(sketch, "E29.13.5.0", {"start": v(-32.54, -26.98) * mm, "end": v(-28.16, -29.38) * mm});
            skLineSegment(sketch, "E29.13.5.1", {"start": v(-28.16, -29.38) * mm, "end": v(-28.04, -34.38) * mm});
            skLineSegment(sketch, "E29.13.5.2", {"start": v(-36.81, -29.58) * mm, "end": v(-32.54, -26.98) * mm});
            skLineSegment(sketch, "E29.13.5.3", {"start": v(-36.7, -34.58) * mm, "end": v(-36.81, -29.58) * mm});
            skLineSegment(sketch, "E29.13.5.4", {"start": v(-32.31, -36.98) * mm, "end": v(-36.7, -34.58) * mm});
            skLineSegment(sketch, "E29.13.5.5", {"start": v(-28.04, -34.38) * mm, "end": v(-32.31, -36.98) * mm});
            skLineSegment(sketch, "E29.13.6.0", {"start": v(-32.43, -46.98) * mm, "end": v(-28.04, -49.38) * mm});
            skLineSegment(sketch, "E29.13.6.1", {"start": v(-28.04, -49.38) * mm, "end": v(-27.93, -54.38) * mm});
            skLineSegment(sketch, "E29.13.6.2", {"start": v(-36.7, -49.58) * mm, "end": v(-32.43, -46.98) * mm});
            skLineSegment(sketch, "E29.13.6.3", {"start": v(-36.59, -54.58) * mm, "end": v(-36.7, -49.58) * mm});
            skLineSegment(sketch, "E29.13.6.4", {"start": v(-32.2, -56.98) * mm, "end": v(-36.59, -54.58) * mm});
            skLineSegment(sketch, "E29.13.6.5", {"start": v(-27.93, -54.38) * mm, "end": v(-32.2, -56.98) * mm});
            skLineSegment(sketch, "E29.14.0.0", {"start": v(-19.11, 73.01) * mm, "end": v(-14.73, 70.61) * mm});
            skLineSegment(sketch, "E29.14.0.1", {"start": v(-14.73, 70.61) * mm, "end": v(-14.61, 65.61) * mm});
            skLineSegment(sketch, "E29.14.0.2", {"start": v(-23.39, 70.41) * mm, "end": v(-19.11, 73.01) * mm});
            skLineSegment(sketch, "E29.14.0.3", {"start": v(-23.27, 65.41) * mm, "end": v(-23.39, 70.41) * mm});
            skLineSegment(sketch, "E29.14.0.4", {"start": v(-18.89, 63.01) * mm, "end": v(-23.27, 65.41) * mm});
            skLineSegment(sketch, "E29.14.0.5", {"start": v(-14.61, 65.61) * mm, "end": v(-18.89, 63.01) * mm});
            skLineSegment(sketch, "E29.14.1.0", {"start": v(-19, 53.01) * mm, "end": v(-14.61, 50.61) * mm});
            skLineSegment(sketch, "E29.14.1.1", {"start": v(-14.61, 50.61) * mm, "end": v(-14.5, 45.61) * mm});
            skLineSegment(sketch, "E29.14.1.2", {"start": v(-23.27, 50.41) * mm, "end": v(-19, 53.01) * mm});
            skLineSegment(sketch, "E29.14.1.3", {"start": v(-23.16, 45.42) * mm, "end": v(-23.27, 50.41) * mm});
            skLineSegment(sketch, "E29.14.1.4", {"start": v(-18.77, 43.02) * mm, "end": v(-23.16, 45.42) * mm});
            skLineSegment(sketch, "E29.14.1.5", {"start": v(-14.5, 45.61) * mm, "end": v(-18.77, 43.02) * mm});
            skLineSegment(sketch, "E29.14.2.0", {"start": v(-18.89, 33.01) * mm, "end": v(-14.5, 30.61) * mm});
            skLineSegment(sketch, "E29.14.2.1", {"start": v(-14.5, 30.61) * mm, "end": v(-14.38, 25.62) * mm});
            skLineSegment(sketch, "E29.14.2.2", {"start": v(-23.16, 30.42) * mm, "end": v(-18.89, 33.01) * mm});
            skLineSegment(sketch, "E29.14.2.3", {"start": v(-23.04, 25.42) * mm, "end": v(-23.16, 30.42) * mm});
            skLineSegment(sketch, "E29.14.2.4", {"start": v(-18.66, 23.02) * mm, "end": v(-23.04, 25.42) * mm});
            skLineSegment(sketch, "E29.14.2.5", {"start": v(-14.38, 25.62) * mm, "end": v(-18.66, 23.02) * mm});
            skLineSegment(sketch, "E29.14.3.0", {"start": v(-18.77, 13.02) * mm, "end": v(-14.38, 10.62) * mm});
            skLineSegment(sketch, "E29.14.3.1", {"start": v(-14.38, 10.62) * mm, "end": v(-14.27, 5.62) * mm});
            skLineSegment(sketch, "E29.14.3.2", {"start": v(-23.04, 10.42) * mm, "end": v(-18.77, 13.02) * mm});
            skLineSegment(sketch, "E29.14.3.3", {"start": v(-22.93, 5.42) * mm, "end": v(-23.04, 10.42) * mm});
            skLineSegment(sketch, "E29.14.3.4", {"start": v(-18.54, 3.02) * mm, "end": v(-22.93, 5.42) * mm});
            skLineSegment(sketch, "E29.14.3.5", {"start": v(-14.27, 5.62) * mm, "end": v(-18.54, 3.02) * mm});
            skLineSegment(sketch, "E29.14.4.0", {"start": v(-18.66, -6.98) * mm, "end": v(-14.27, -9.38) * mm});
            skLineSegment(sketch, "E29.14.4.1", {"start": v(-14.27, -9.38) * mm, "end": v(-14.16, -14.38) * mm});
            skLineSegment(sketch, "E29.14.4.2", {"start": v(-22.93, -9.58) * mm, "end": v(-18.66, -6.98) * mm});
            skLineSegment(sketch, "E29.14.4.3", {"start": v(-22.81, -14.58) * mm, "end": v(-22.93, -9.58) * mm});
            skLineSegment(sketch, "E29.14.4.4", {"start": v(-18.43, -16.98) * mm, "end": v(-22.81, -14.58) * mm});
            skLineSegment(sketch, "E29.14.4.5", {"start": v(-14.16, -14.38) * mm, "end": v(-18.43, -16.98) * mm});
            skLineSegment(sketch, "E29.14.5.0", {"start": v(-18.54, -26.98) * mm, "end": v(-14.16, -29.38) * mm});
            skLineSegment(sketch, "E29.14.5.1", {"start": v(-14.16, -29.38) * mm, "end": v(-14.04, -34.38) * mm});
            skLineSegment(sketch, "E29.14.5.2", {"start": v(-22.81, -29.58) * mm, "end": v(-18.54, -26.98) * mm});
            skLineSegment(sketch, "E29.14.5.3", {"start": v(-22.7, -34.58) * mm, "end": v(-22.81, -29.58) * mm});
            skLineSegment(sketch, "E29.14.5.4", {"start": v(-18.31, -36.98) * mm, "end": v(-22.7, -34.58) * mm});
            skLineSegment(sketch, "E29.14.5.5", {"start": v(-14.04, -34.38) * mm, "end": v(-18.31, -36.98) * mm});
            skLineSegment(sketch, "E29.14.6.0", {"start": v(-18.43, -46.98) * mm, "end": v(-14.04, -49.38) * mm});
            skLineSegment(sketch, "E29.14.6.1", {"start": v(-14.04, -49.38) * mm, "end": v(-13.93, -54.38) * mm});
            skLineSegment(sketch, "E29.14.6.2", {"start": v(-22.7, -49.58) * mm, "end": v(-18.43, -46.98) * mm});
            skLineSegment(sketch, "E29.14.6.3", {"start": v(-22.59, -54.58) * mm, "end": v(-22.7, -49.58) * mm});
            skLineSegment(sketch, "E29.14.6.4", {"start": v(-18.2, -56.98) * mm, "end": v(-22.59, -54.58) * mm});
            skLineSegment(sketch, "E29.14.6.5", {"start": v(-13.93, -54.38) * mm, "end": v(-18.2, -56.98) * mm});
            skLineSegment(sketch, "E29.15.0.0", {"start": v(-5.11, 73.01) * mm, "end": v(-0.73, 70.61) * mm});
            skLineSegment(sketch, "E29.15.0.1", {"start": v(-0.73, 70.61) * mm, "end": v(-0.61, 65.61) * mm});
            skLineSegment(sketch, "E29.15.0.2", {"start": v(-9.39, 70.41) * mm, "end": v(-5.11, 73.01) * mm});
            skLineSegment(sketch, "E29.15.0.3", {"start": v(-9.27, 65.42) * mm, "end": v(-9.39, 70.41) * mm});
            skLineSegment(sketch, "E29.15.0.4", {"start": v(-4.89, 63.01) * mm, "end": v(-9.27, 65.42) * mm});
            skLineSegment(sketch, "E29.15.0.5", {"start": v(-0.61, 65.61) * mm, "end": v(-4.89, 63.01) * mm});
            skLineSegment(sketch, "E29.15.1.0", {"start": v(-5, 53.01) * mm, "end": v(-0.61, 50.61) * mm});
            skLineSegment(sketch, "E29.15.1.1", {"start": v(-0.61, 50.61) * mm, "end": v(-0.5, 45.61) * mm});
            skLineSegment(sketch, "E29.15.1.2", {"start": v(-9.27, 50.42) * mm, "end": v(-5, 53.01) * mm});
            skLineSegment(sketch, "E29.15.1.3", {"start": v(-9.16, 45.42) * mm, "end": v(-9.27, 50.42) * mm});
            skLineSegment(sketch, "E29.15.1.4", {"start": v(-4.77, 43.02) * mm, "end": v(-9.16, 45.42) * mm});
            skLineSegment(sketch, "E29.15.1.5", {"start": v(-0.5, 45.61) * mm, "end": v(-4.77, 43.02) * mm});
            skLineSegment(sketch, "E29.15.2.0", {"start": v(-4.89, 33.01) * mm, "end": v(-0.5, 30.61) * mm});
            skLineSegment(sketch, "E29.15.2.1", {"start": v(-0.5, 30.61) * mm, "end": v(-0.38, 25.62) * mm});
            skLineSegment(sketch, "E29.15.2.2", {"start": v(-9.16, 30.42) * mm, "end": v(-4.89, 33.01) * mm});
            skLineSegment(sketch, "E29.15.2.3", {"start": v(-9.04, 25.42) * mm, "end": v(-9.16, 30.42) * mm});
            skLineSegment(sketch, "E29.15.2.4", {"start": v(-4.66, 23.02) * mm, "end": v(-9.04, 25.42) * mm});
            skLineSegment(sketch, "E29.15.2.5", {"start": v(-0.38, 25.62) * mm, "end": v(-4.66, 23.02) * mm});
            skLineSegment(sketch, "E29.15.3.0", {"start": v(-4.77, 13.02) * mm, "end": v(-0.38, 10.62) * mm});
            skLineSegment(sketch, "E29.15.3.1", {"start": v(-0.38, 10.62) * mm, "end": v(-0.27, 5.62) * mm});
            skLineSegment(sketch, "E29.15.3.2", {"start": v(-9.04, 10.42) * mm, "end": v(-4.77, 13.02) * mm});
            skLineSegment(sketch, "E29.15.3.3", {"start": v(-8.93, 5.42) * mm, "end": v(-9.04, 10.42) * mm});
            skLineSegment(sketch, "E29.15.3.4", {"start": v(-4.54, 3.02) * mm, "end": v(-8.93, 5.42) * mm});
            skLineSegment(sketch, "E29.15.3.5", {"start": v(-0.27, 5.62) * mm, "end": v(-4.54, 3.02) * mm});
            skLineSegment(sketch, "E29.15.4.0", {"start": v(-4.66, -6.98) * mm, "end": v(-0.27, -9.38) * mm});
            skLineSegment(sketch, "E29.15.4.1", {"start": v(-0.27, -9.38) * mm, "end": v(-0.16, -14.38) * mm});
            skLineSegment(sketch, "E29.15.4.2", {"start": v(-8.93, -9.58) * mm, "end": v(-4.66, -6.98) * mm});
            skLineSegment(sketch, "E29.15.4.3", {"start": v(-8.81, -14.58) * mm, "end": v(-8.93, -9.58) * mm});
            skLineSegment(sketch, "E29.15.4.4", {"start": v(-4.43, -16.98) * mm, "end": v(-8.81, -14.58) * mm});
            skLineSegment(sketch, "E29.15.4.5", {"start": v(-0.16, -14.38) * mm, "end": v(-4.43, -16.98) * mm});
            skLineSegment(sketch, "E29.15.5.0", {"start": v(-4.54, -26.98) * mm, "end": v(-0.16, -29.38) * mm});
            skLineSegment(sketch, "E29.15.5.1", {"start": v(-0.16, -29.38) * mm, "end": v(-0.04, -34.38) * mm});
            skLineSegment(sketch, "E29.15.5.2", {"start": v(-8.81, -29.58) * mm, "end": v(-4.54, -26.98) * mm});
            skLineSegment(sketch, "E29.15.5.3", {"start": v(-8.7, -34.58) * mm, "end": v(-8.81, -29.58) * mm});
            skLineSegment(sketch, "E29.15.5.4", {"start": v(-4.31, -36.98) * mm, "end": v(-8.7, -34.58) * mm});
            skLineSegment(sketch, "E29.15.5.5", {"start": v(-0.04, -34.38) * mm, "end": v(-4.31, -36.98) * mm});
            skLineSegment(sketch, "E29.15.6.0", {"start": v(-4.43, -46.98) * mm, "end": v(-0.04, -49.38) * mm});
            skLineSegment(sketch, "E29.15.6.1", {"start": v(-0.04, -49.38) * mm, "end": v(0.07, -54.38) * mm});
            skLineSegment(sketch, "E29.15.6.2", {"start": v(-8.7, -49.58) * mm, "end": v(-4.43, -46.98) * mm});
            skLineSegment(sketch, "E29.15.6.3", {"start": v(-8.59, -54.58) * mm, "end": v(-8.7, -49.58) * mm});
            skLineSegment(sketch, "E29.15.6.4", {"start": v(-4.2, -56.98) * mm, "end": v(-8.59, -54.58) * mm});
            skLineSegment(sketch, "E29.15.6.5", {"start": v(0.07, -54.38) * mm, "end": v(-4.2, -56.98) * mm});
            skLineSegment(sketch, "E29.16.0.0", {"start": v(8.89, 73.01) * mm, "end": v(13.27, 70.61) * mm});
            skLineSegment(sketch, "E29.16.0.1", {"start": v(13.27, 70.61) * mm, "end": v(13.39, 65.61) * mm});
            skLineSegment(sketch, "E29.16.0.2", {"start": v(4.61, 70.41) * mm, "end": v(8.89, 73.01) * mm});
            skLineSegment(sketch, "E29.16.0.3", {"start": v(4.73, 65.42) * mm, "end": v(4.61, 70.41) * mm});
            skLineSegment(sketch, "E29.16.0.4", {"start": v(9.11, 63.02) * mm, "end": v(4.73, 65.42) * mm});
            skLineSegment(sketch, "E29.16.0.5", {"start": v(13.39, 65.61) * mm, "end": v(9.11, 63.02) * mm});
            skLineSegment(sketch, "E29.16.1.0", {"start": v(9, 53.01) * mm, "end": v(13.39, 50.61) * mm});
            skLineSegment(sketch, "E29.16.1.1", {"start": v(13.39, 50.61) * mm, "end": v(13.5, 45.62) * mm});
            skLineSegment(sketch, "E29.16.1.2", {"start": v(4.73, 50.42) * mm, "end": v(9, 53.01) * mm});
            skLineSegment(sketch, "E29.16.1.3", {"start": v(4.84, 45.42) * mm, "end": v(4.73, 50.42) * mm});
            skLineSegment(sketch, "E29.16.1.4", {"start": v(9.23, 43.02) * mm, "end": v(4.84, 45.42) * mm});
            skLineSegment(sketch, "E29.16.1.5", {"start": v(13.5, 45.62) * mm, "end": v(9.23, 43.02) * mm});
            skLineSegment(sketch, "E29.16.2.0", {"start": v(9.11, 33.02) * mm, "end": v(13.5, 30.62) * mm});
            skLineSegment(sketch, "E29.16.2.1", {"start": v(13.5, 30.62) * mm, "end": v(13.62, 25.62) * mm});
            skLineSegment(sketch, "E29.16.2.2", {"start": v(4.84, 30.42) * mm, "end": v(9.11, 33.02) * mm});
            skLineSegment(sketch, "E29.16.2.3", {"start": v(4.96, 25.42) * mm, "end": v(4.84, 30.42) * mm});
            skLineSegment(sketch, "E29.16.2.4", {"start": v(9.34, 23.02) * mm, "end": v(4.96, 25.42) * mm});
            skLineSegment(sketch, "E29.16.2.5", {"start": v(13.62, 25.62) * mm, "end": v(9.34, 23.02) * mm});
            skLineSegment(sketch, "E29.16.3.0", {"start": v(9.23, 13.02) * mm, "end": v(13.62, 10.62) * mm});
            skLineSegment(sketch, "E29.16.3.1", {"start": v(13.62, 10.62) * mm, "end": v(13.73, 5.62) * mm});
            skLineSegment(sketch, "E29.16.3.2", {"start": v(4.96, 10.42) * mm, "end": v(9.23, 13.02) * mm});
            skLineSegment(sketch, "E29.16.3.3", {"start": v(5.07, 5.42) * mm, "end": v(4.96, 10.42) * mm});
            skLineSegment(sketch, "E29.16.3.4", {"start": v(9.46, 3.02) * mm, "end": v(5.07, 5.42) * mm});
            skLineSegment(sketch, "E29.16.3.5", {"start": v(13.73, 5.62) * mm, "end": v(9.46, 3.02) * mm});
            skLineSegment(sketch, "E29.16.4.0", {"start": v(9.34, -6.98) * mm, "end": v(13.73, -9.38) * mm});
            skLineSegment(sketch, "E29.16.4.1", {"start": v(13.73, -9.38) * mm, "end": v(13.84, -14.38) * mm});
            skLineSegment(sketch, "E29.16.4.2", {"start": v(5.07, -9.58) * mm, "end": v(9.34, -6.98) * mm});
            skLineSegment(sketch, "E29.16.4.3", {"start": v(5.19, -14.58) * mm, "end": v(5.07, -9.58) * mm});
            skLineSegment(sketch, "E29.16.4.4", {"start": v(9.57, -16.98) * mm, "end": v(5.19, -14.58) * mm});
            skLineSegment(sketch, "E29.16.4.5", {"start": v(13.84, -14.38) * mm, "end": v(9.57, -16.98) * mm});
            skLineSegment(sketch, "E29.16.5.0", {"start": v(9.46, -26.98) * mm, "end": v(13.84, -29.38) * mm});
            skLineSegment(sketch, "E29.16.5.1", {"start": v(13.84, -29.38) * mm, "end": v(13.96, -34.38) * mm});
            skLineSegment(sketch, "E29.16.5.2", {"start": v(5.19, -29.58) * mm, "end": v(9.46, -26.98) * mm});
            skLineSegment(sketch, "E29.16.5.3", {"start": v(5.3, -34.58) * mm, "end": v(5.19, -29.58) * mm});
            skLineSegment(sketch, "E29.16.5.4", {"start": v(9.69, -36.98) * mm, "end": v(5.3, -34.58) * mm});
            skLineSegment(sketch, "E29.16.5.5", {"start": v(13.96, -34.38) * mm, "end": v(9.69, -36.98) * mm});
            skLineSegment(sketch, "E29.16.6.0", {"start": v(9.57, -46.98) * mm, "end": v(13.96, -49.38) * mm});
            skLineSegment(sketch, "E29.16.6.1", {"start": v(13.96, -49.38) * mm, "end": v(14.07, -54.38) * mm});
            skLineSegment(sketch, "E29.16.6.2", {"start": v(5.3, -49.58) * mm, "end": v(9.57, -46.98) * mm});
            skLineSegment(sketch, "E29.16.6.3", {"start": v(5.41, -54.58) * mm, "end": v(5.3, -49.58) * mm});
            skLineSegment(sketch, "E29.16.6.4", {"start": v(9.8, -56.98) * mm, "end": v(5.41, -54.58) * mm});
            skLineSegment(sketch, "E29.16.6.5", {"start": v(14.07, -54.38) * mm, "end": v(9.8, -56.98) * mm});
            skLineSegment(sketch, "E29.17.0.0", {"start": v(22.89, 73.01) * mm, "end": v(27.27, 70.61) * mm});
            skLineSegment(sketch, "E29.17.0.1", {"start": v(27.27, 70.61) * mm, "end": v(27.39, 65.62) * mm});
            skLineSegment(sketch, "E29.17.0.2", {"start": v(18.61, 70.42) * mm, "end": v(22.89, 73.01) * mm});
            skLineSegment(sketch, "E29.17.0.3", {"start": v(18.73, 65.42) * mm, "end": v(18.61, 70.42) * mm});
            skLineSegment(sketch, "E29.17.0.4", {"start": v(23.11, 63.02) * mm, "end": v(18.73, 65.42) * mm});
            skLineSegment(sketch, "E29.17.0.5", {"start": v(27.39, 65.62) * mm, "end": v(23.11, 63.02) * mm});
            skLineSegment(sketch, "E29.17.1.0", {"start": v(23, 53.02) * mm, "end": v(27.39, 50.62) * mm});
            skLineSegment(sketch, "E29.17.1.1", {"start": v(27.39, 50.62) * mm, "end": v(27.5, 45.62) * mm});
            skLineSegment(sketch, "E29.17.1.2", {"start": v(18.73, 50.42) * mm, "end": v(23, 53.02) * mm});
            skLineSegment(sketch, "E29.17.1.3", {"start": v(18.84, 45.42) * mm, "end": v(18.73, 50.42) * mm});
            skLineSegment(sketch, "E29.17.1.4", {"start": v(23.23, 43.02) * mm, "end": v(18.84, 45.42) * mm});
            skLineSegment(sketch, "E29.17.1.5", {"start": v(27.5, 45.62) * mm, "end": v(23.23, 43.02) * mm});
            skLineSegment(sketch, "E29.17.2.0", {"start": v(23.11, 33.02) * mm, "end": v(27.5, 30.62) * mm});
            skLineSegment(sketch, "E29.17.2.1", {"start": v(27.5, 30.62) * mm, "end": v(27.62, 25.62) * mm});
            skLineSegment(sketch, "E29.17.2.2", {"start": v(18.84, 30.42) * mm, "end": v(23.11, 33.02) * mm});
            skLineSegment(sketch, "E29.17.2.3", {"start": v(18.96, 25.42) * mm, "end": v(18.84, 30.42) * mm});
            skLineSegment(sketch, "E29.17.2.4", {"start": v(23.34, 23.02) * mm, "end": v(18.96, 25.42) * mm});
            skLineSegment(sketch, "E29.17.2.5", {"start": v(27.62, 25.62) * mm, "end": v(23.34, 23.02) * mm});
            skLineSegment(sketch, "E29.17.3.0", {"start": v(23.23, 13.02) * mm, "end": v(27.62, 10.62) * mm});
            skLineSegment(sketch, "E29.17.3.1", {"start": v(27.62, 10.62) * mm, "end": v(27.73, 5.62) * mm});
            skLineSegment(sketch, "E29.17.3.2", {"start": v(18.96, 10.42) * mm, "end": v(23.23, 13.02) * mm});
            skLineSegment(sketch, "E29.17.3.3", {"start": v(19.07, 5.42) * mm, "end": v(18.96, 10.42) * mm});
            skLineSegment(sketch, "E29.17.3.4", {"start": v(23.46, 3.02) * mm, "end": v(19.07, 5.42) * mm});
            skLineSegment(sketch, "E29.17.3.5", {"start": v(27.73, 5.62) * mm, "end": v(23.46, 3.02) * mm});
            skLineSegment(sketch, "E29.17.4.0", {"start": v(23.34, -6.98) * mm, "end": v(27.73, -9.38) * mm});
            skLineSegment(sketch, "E29.17.4.1", {"start": v(27.73, -9.38) * mm, "end": v(27.84, -14.38) * mm});
            skLineSegment(sketch, "E29.17.4.2", {"start": v(19.07, -9.58) * mm, "end": v(23.34, -6.98) * mm});
            skLineSegment(sketch, "E29.17.4.3", {"start": v(19.19, -14.58) * mm, "end": v(19.07, -9.58) * mm});
            skLineSegment(sketch, "E29.17.4.4", {"start": v(23.57, -16.98) * mm, "end": v(19.19, -14.58) * mm});
            skLineSegment(sketch, "E29.17.4.5", {"start": v(27.84, -14.38) * mm, "end": v(23.57, -16.98) * mm});
            skLineSegment(sketch, "E29.17.5.0", {"start": v(23.46, -26.98) * mm, "end": v(27.84, -29.38) * mm});
            skLineSegment(sketch, "E29.17.5.1", {"start": v(27.84, -29.38) * mm, "end": v(27.96, -34.38) * mm});
            skLineSegment(sketch, "E29.17.5.2", {"start": v(19.19, -29.58) * mm, "end": v(23.46, -26.98) * mm});
            skLineSegment(sketch, "E29.17.5.3", {"start": v(19.3, -34.58) * mm, "end": v(19.19, -29.58) * mm});
            skLineSegment(sketch, "E29.17.5.4", {"start": v(23.69, -36.98) * mm, "end": v(19.3, -34.58) * mm});
            skLineSegment(sketch, "E29.17.5.5", {"start": v(27.96, -34.38) * mm, "end": v(23.69, -36.98) * mm});
            skLineSegment(sketch, "E29.17.6.0", {"start": v(23.57, -46.98) * mm, "end": v(27.96, -49.38) * mm});
            skLineSegment(sketch, "E29.17.6.1", {"start": v(27.96, -49.38) * mm, "end": v(28.07, -54.38) * mm});
            skLineSegment(sketch, "E29.17.6.2", {"start": v(19.3, -49.58) * mm, "end": v(23.57, -46.98) * mm});
            skLineSegment(sketch, "E29.17.6.3", {"start": v(19.41, -54.58) * mm, "end": v(19.3, -49.58) * mm});
            skLineSegment(sketch, "E29.17.6.4", {"start": v(23.8, -56.98) * mm, "end": v(19.41, -54.58) * mm});
            skLineSegment(sketch, "E29.17.6.5", {"start": v(28.07, -54.38) * mm, "end": v(23.8, -56.98) * mm});
            skLineSegment(sketch, "E29.18.0.0", {"start": v(36.89, 73.02) * mm, "end": v(41.27, 70.61) * mm});
            skLineSegment(sketch, "E29.18.0.1", {"start": v(41.27, 70.61) * mm, "end": v(41.39, 65.62) * mm});
            skLineSegment(sketch, "E29.18.0.2", {"start": v(32.61, 70.42) * mm, "end": v(36.89, 73.02) * mm});
            skLineSegment(sketch, "E29.18.0.3", {"start": v(32.73, 65.42) * mm, "end": v(32.61, 70.42) * mm});
            skLineSegment(sketch, "E29.18.0.4", {"start": v(37.11, 63.02) * mm, "end": v(32.73, 65.42) * mm});
            skLineSegment(sketch, "E29.18.0.5", {"start": v(41.39, 65.62) * mm, "end": v(37.11, 63.02) * mm});
            skLineSegment(sketch, "E29.18.1.0", {"start": v(37, 53.02) * mm, "end": v(41.39, 50.62) * mm});
            skLineSegment(sketch, "E29.18.1.1", {"start": v(41.39, 50.62) * mm, "end": v(41.5, 45.62) * mm});
            skLineSegment(sketch, "E29.18.1.2", {"start": v(32.73, 50.42) * mm, "end": v(37, 53.02) * mm});
            skLineSegment(sketch, "E29.18.1.3", {"start": v(32.84, 45.42) * mm, "end": v(32.73, 50.42) * mm});
            skLineSegment(sketch, "E29.18.1.4", {"start": v(37.23, 43.02) * mm, "end": v(32.84, 45.42) * mm});
            skLineSegment(sketch, "E29.18.1.5", {"start": v(41.5, 45.62) * mm, "end": v(37.23, 43.02) * mm});
            skLineSegment(sketch, "E29.18.2.0", {"start": v(37.11, 33.02) * mm, "end": v(41.5, 30.62) * mm});
            skLineSegment(sketch, "E29.18.2.1", {"start": v(41.5, 30.62) * mm, "end": v(41.62, 25.62) * mm});
            skLineSegment(sketch, "E29.18.2.2", {"start": v(32.84, 30.42) * mm, "end": v(37.11, 33.02) * mm});
            skLineSegment(sketch, "E29.18.2.3", {"start": v(32.96, 25.42) * mm, "end": v(32.84, 30.42) * mm});
            skLineSegment(sketch, "E29.18.2.4", {"start": v(37.34, 23.02) * mm, "end": v(32.96, 25.42) * mm});
            skLineSegment(sketch, "E29.18.2.5", {"start": v(41.62, 25.62) * mm, "end": v(37.34, 23.02) * mm});
            skLineSegment(sketch, "E29.18.3.0", {"start": v(37.23, 13.02) * mm, "end": v(41.62, 10.62) * mm});
            skLineSegment(sketch, "E29.18.3.1", {"start": v(41.62, 10.62) * mm, "end": v(41.73, 5.62) * mm});
            skLineSegment(sketch, "E29.18.3.2", {"start": v(32.96, 10.42) * mm, "end": v(37.23, 13.02) * mm});
            skLineSegment(sketch, "E29.18.3.3", {"start": v(33.07, 5.42) * mm, "end": v(32.96, 10.42) * mm});
            skLineSegment(sketch, "E29.18.3.4", {"start": v(37.46, 3.02) * mm, "end": v(33.07, 5.42) * mm});
            skLineSegment(sketch, "E29.18.3.5", {"start": v(41.73, 5.62) * mm, "end": v(37.46, 3.02) * mm});
            skLineSegment(sketch, "E29.18.4.0", {"start": v(37.34, -6.98) * mm, "end": v(41.73, -9.38) * mm});
            skLineSegment(sketch, "E29.18.4.1", {"start": v(41.73, -9.38) * mm, "end": v(41.84, -14.38) * mm});
            skLineSegment(sketch, "E29.18.4.2", {"start": v(33.07, -9.58) * mm, "end": v(37.34, -6.98) * mm});
            skLineSegment(sketch, "E29.18.4.3", {"start": v(33.19, -14.58) * mm, "end": v(33.07, -9.58) * mm});
            skLineSegment(sketch, "E29.18.4.4", {"start": v(37.57, -16.98) * mm, "end": v(33.19, -14.58) * mm});
            skLineSegment(sketch, "E29.18.4.5", {"start": v(41.84, -14.38) * mm, "end": v(37.57, -16.98) * mm});
            skLineSegment(sketch, "E29.18.5.0", {"start": v(37.46, -26.98) * mm, "end": v(41.84, -29.38) * mm});
            skLineSegment(sketch, "E29.18.5.1", {"start": v(41.84, -29.38) * mm, "end": v(41.96, -34.38) * mm});
            skLineSegment(sketch, "E29.18.5.2", {"start": v(33.19, -29.58) * mm, "end": v(37.46, -26.98) * mm});
            skLineSegment(sketch, "E29.18.5.3", {"start": v(33.3, -34.58) * mm, "end": v(33.19, -29.58) * mm});
            skLineSegment(sketch, "E29.18.5.4", {"start": v(37.69, -36.98) * mm, "end": v(33.3, -34.58) * mm});
            skLineSegment(sketch, "E29.18.5.5", {"start": v(41.96, -34.38) * mm, "end": v(37.69, -36.98) * mm});
            skLineSegment(sketch, "E29.18.6.0", {"start": v(37.57, -46.98) * mm, "end": v(41.96, -49.38) * mm});
            skLineSegment(sketch, "E29.18.6.1", {"start": v(41.96, -49.38) * mm, "end": v(42.07, -54.38) * mm});
            skLineSegment(sketch, "E29.18.6.2", {"start": v(33.3, -49.58) * mm, "end": v(37.57, -46.98) * mm});
            skLineSegment(sketch, "E29.18.6.3", {"start": v(33.41, -54.57) * mm, "end": v(33.3, -49.58) * mm});
            skLineSegment(sketch, "E29.18.6.4", {"start": v(37.8, -56.97) * mm, "end": v(33.41, -54.57) * mm});
            skLineSegment(sketch, "E29.18.6.5", {"start": v(42.07, -54.38) * mm, "end": v(37.8, -56.97) * mm});
            skLineSegment(sketch, "E29.19.0.0", {"start": v(50.89, 73.02) * mm, "end": v(55.27, 70.62) * mm});
            skLineSegment(sketch, "E29.19.0.1", {"start": v(55.27, 70.62) * mm, "end": v(55.39, 65.62) * mm});
            skLineSegment(sketch, "E29.19.0.2", {"start": v(46.61, 70.42) * mm, "end": v(50.89, 73.02) * mm});
            skLineSegment(sketch, "E29.19.0.3", {"start": v(46.73, 65.42) * mm, "end": v(46.61, 70.42) * mm});
            skLineSegment(sketch, "E29.19.0.4", {"start": v(51.11, 63.02) * mm, "end": v(46.73, 65.42) * mm});
            skLineSegment(sketch, "E29.19.0.5", {"start": v(55.39, 65.62) * mm, "end": v(51.11, 63.02) * mm});
            skLineSegment(sketch, "E29.19.1.0", {"start": v(51, 53.02) * mm, "end": v(55.39, 50.62) * mm});
            skLineSegment(sketch, "E29.19.1.1", {"start": v(55.39, 50.62) * mm, "end": v(55.5, 45.62) * mm});
            skLineSegment(sketch, "E29.19.1.2", {"start": v(46.73, 50.42) * mm, "end": v(51, 53.02) * mm});
            skLineSegment(sketch, "E29.19.1.3", {"start": v(46.84, 45.42) * mm, "end": v(46.73, 50.42) * mm});
            skLineSegment(sketch, "E29.19.1.4", {"start": v(51.23, 43.02) * mm, "end": v(46.84, 45.42) * mm});
            skLineSegment(sketch, "E29.19.1.5", {"start": v(55.5, 45.62) * mm, "end": v(51.23, 43.02) * mm});
            skLineSegment(sketch, "E29.19.2.0", {"start": v(51.11, 33.02) * mm, "end": v(55.5, 30.62) * mm});
            skLineSegment(sketch, "E29.19.2.1", {"start": v(55.5, 30.62) * mm, "end": v(55.62, 25.62) * mm});
            skLineSegment(sketch, "E29.19.2.2", {"start": v(46.84, 30.42) * mm, "end": v(51.11, 33.02) * mm});
            skLineSegment(sketch, "E29.19.2.3", {"start": v(46.96, 25.42) * mm, "end": v(46.84, 30.42) * mm});
            skLineSegment(sketch, "E29.19.2.4", {"start": v(51.34, 23.02) * mm, "end": v(46.96, 25.42) * mm});
            skLineSegment(sketch, "E29.19.2.5", {"start": v(55.62, 25.62) * mm, "end": v(51.34, 23.02) * mm});
            skLineSegment(sketch, "E29.19.3.0", {"start": v(51.23, 13.02) * mm, "end": v(55.62, 10.62) * mm});
            skLineSegment(sketch, "E29.19.3.1", {"start": v(55.62, 10.62) * mm, "end": v(55.73, 5.62) * mm});
            skLineSegment(sketch, "E29.19.3.2", {"start": v(46.96, 10.42) * mm, "end": v(51.23, 13.02) * mm});
            skLineSegment(sketch, "E29.19.3.3", {"start": v(47.07, 5.42) * mm, "end": v(46.96, 10.42) * mm});
            skLineSegment(sketch, "E29.19.3.4", {"start": v(51.46, 3.02) * mm, "end": v(47.07, 5.42) * mm});
            skLineSegment(sketch, "E29.19.3.5", {"start": v(55.73, 5.62) * mm, "end": v(51.46, 3.02) * mm});
            skLineSegment(sketch, "E29.19.4.0", {"start": v(51.34, -6.98) * mm, "end": v(55.73, -9.38) * mm});
            skLineSegment(sketch, "E29.19.4.1", {"start": v(55.73, -9.38) * mm, "end": v(55.84, -14.38) * mm});
            skLineSegment(sketch, "E29.19.4.2", {"start": v(47.07, -9.58) * mm, "end": v(51.34, -6.98) * mm});
            skLineSegment(sketch, "E29.19.4.3", {"start": v(47.19, -14.58) * mm, "end": v(47.07, -9.58) * mm});
            skLineSegment(sketch, "E29.19.4.4", {"start": v(51.57, -16.98) * mm, "end": v(47.19, -14.58) * mm});
            skLineSegment(sketch, "E29.19.4.5", {"start": v(55.84, -14.38) * mm, "end": v(51.57, -16.98) * mm});
            skLineSegment(sketch, "E29.19.5.0", {"start": v(51.46, -26.98) * mm, "end": v(55.84, -29.38) * mm});
            skLineSegment(sketch, "E29.19.5.1", {"start": v(55.84, -29.38) * mm, "end": v(55.96, -34.38) * mm});
            skLineSegment(sketch, "E29.19.5.2", {"start": v(47.19, -29.58) * mm, "end": v(51.46, -26.98) * mm});
            skLineSegment(sketch, "E29.19.5.3", {"start": v(47.3, -34.57) * mm, "end": v(47.19, -29.58) * mm});
            skLineSegment(sketch, "E29.19.5.4", {"start": v(51.69, -36.97) * mm, "end": v(47.3, -34.57) * mm});
            skLineSegment(sketch, "E29.19.5.5", {"start": v(55.96, -34.38) * mm, "end": v(51.69, -36.97) * mm});
            skLineSegment(sketch, "E29.19.6.0", {"start": v(51.57, -46.98) * mm, "end": v(55.96, -49.38) * mm});
            skLineSegment(sketch, "E29.19.6.1", {"start": v(55.96, -49.38) * mm, "end": v(56.07, -54.38) * mm});
            skLineSegment(sketch, "E29.19.6.2", {"start": v(47.3, -49.57) * mm, "end": v(51.57, -46.98) * mm});
            skLineSegment(sketch, "E29.19.6.3", {"start": v(47.41, -54.57) * mm, "end": v(47.3, -49.57) * mm});
            skLineSegment(sketch, "E29.19.6.4", {"start": v(51.8, -56.97) * mm, "end": v(47.41, -54.57) * mm});
            skLineSegment(sketch, "E29.19.6.5", {"start": v(56.07, -54.38) * mm, "end": v(51.8, -56.97) * mm});
            skLineSegment(sketch, "E29.direction1", {"start": v(-215.11, 73) * mm, "end": v(-201.11, 73) * mm, "construction": true});
            skLineSegment(sketch, "E29.direction2", {"start": v(-215.11, 73) * mm, "end": v(-215, 53) * mm, "construction": true});
            skLineSegment(sketch, "E30.MirrorCS", {"start": v(-235.11, 63) * mm, "end": v(-230.73, 65.4) * mm});
            skLineSegment(sketch, "E31.MirrorCS", {"start": v(-351.73, -9.39) * mm, "end": v(-351.84, -14.39) * mm});
            skLineSegment(sketch, "E32.MirrorCS", {"start": v(-239.39, 65.6) * mm, "end": v(-235.11, 63) * mm});
            skLineSegment(sketch, "E33.MirrorCS", {"start": v(-351.96, -49.39) * mm, "end": v(-352.07, -54.39) * mm});
            skLineSegment(sketch, "E34.MirrorCS", {"start": v(-230.61, 70.4) * mm, "end": v(-234.89, 73) * mm});
            skLineSegment(sketch, "E35.MirrorCS", {"start": v(-244.61, 70.4) * mm, "end": v(-248.89, 73) * mm});
            skLineSegment(sketch, "E36.MirrorCS", {"start": v(-234.89, 73) * mm, "end": v(-239.27, 70.6) * mm});
            skLineSegment(sketch, "E37.MirrorCS", {"start": v(-239.27, 70.6) * mm, "end": v(-239.39, 65.6) * mm});
            skLineSegment(sketch, "E38.MirrorCS", {"start": v(-291, 53) * mm, "end": v(-295.39, 50.6) * mm});
            skLineSegment(sketch, "E39.MirrorCS", {"start": v(-272.73, 65.4) * mm, "end": v(-272.61, 70.4) * mm});
            skLineSegment(sketch, "E40.MirrorCS", {"start": v(-333.11, 33) * mm, "end": v(-337.5, 30.6) * mm});
            skLineSegment(sketch, "E41.MirrorCS", {"start": v(-249.34, -7) * mm, "end": v(-253.73, -9.4) * mm});
            skLineSegment(sketch, "E42.MirrorCS", {"start": v(-235.23, 13) * mm, "end": v(-239.62, 10.6) * mm});
            skLineSegment(sketch, "E43.MirrorCS", {"start": v(-305.46, -27) * mm, "end": v(-309.84, -29.4) * mm});
            skLineSegment(sketch, "E44.MirrorCS", {"start": v(-267.84, -29.4) * mm, "end": v(-267.96, -34.4) * mm});
            skLineSegment(sketch, "E45.MirrorCS", {"start": v(-277.23, 13) * mm, "end": v(-281.62, 10.6) * mm});
            skLineSegment(sketch, "E46.MirrorCS", {"start": v(-267.73, -9.4) * mm, "end": v(-267.84, -14.4) * mm});
            skLineSegment(sketch, "E47.MirrorCS", {"start": v(-333.34, -6.99) * mm, "end": v(-337.73, -9.39) * mm});
            skLineSegment(sketch, "E48.MirrorCS", {"start": v(-315.41, -54.59) * mm, "end": v(-315.3, -49.59) * mm});
            skLineSegment(sketch, "E49.MirrorCS", {"start": v(-263.57, -17) * mm, "end": v(-259.19, -14.6) * mm});
            skLineSegment(sketch, "E50.MirrorCS", {"start": v(-249.11, 63) * mm, "end": v(-244.73, 65.4) * mm});
            skLineSegment(sketch, "E51.MirrorCS", {"start": v(-245.41, -54.59) * mm, "end": v(-245.3, -49.6) * mm});
            skLineSegment(sketch, "E52.MirrorCS", {"start": v(-323.39, 50.6) * mm, "end": v(-323.5, 45.6) * mm});
            skLineSegment(sketch, "E53.MirrorCS", {"start": v(-281.27, 70.6) * mm, "end": v(-281.39, 65.6) * mm});
            skLineSegment(sketch, "E54.MirrorCS", {"start": v(-281.62, 10.6) * mm, "end": v(-281.73, 5.6) * mm});
            skLineSegment(sketch, "E55.MirrorCS", {"start": v(-291.34, -7) * mm, "end": v(-295.73, -9.4) * mm});
            skLineSegment(sketch, "E56.MirrorCS", {"start": v(-305.34, 23) * mm, "end": v(-300.96, 25.4) * mm});
            skLineSegment(sketch, "E57.MirrorCS", {"start": v(-267.84, -14.4) * mm, "end": v(-263.57, -17) * mm});
            skLineSegment(sketch, "E58.MirrorCS", {"start": v(-235, 53) * mm, "end": v(-239.39, 50.6) * mm});
            skLineSegment(sketch, "E59.MirrorCS", {"start": v(-249, 53) * mm, "end": v(-253.39, 50.6) * mm});
            skLineSegment(sketch, "E60.MirrorCS", {"start": v(-337.84, -14.39) * mm, "end": v(-333.57, -16.99) * mm});
            skLineSegment(sketch, "E61.MirrorCS", {"start": v(-343.3, -34.58) * mm, "end": v(-343.19, -29.59) * mm});
            skLineSegment(sketch, "E62.MirrorCS", {"start": v(-319, 53) * mm, "end": v(-323.39, 50.6) * mm});
            skLineSegment(sketch, "E63.MirrorCS", {"start": v(-244.84, 45.4) * mm, "end": v(-244.73, 50.4) * mm});
            skLineSegment(sketch, "E64.MirrorCS", {"start": v(-319.57, -46.99) * mm, "end": v(-323.96, -49.39) * mm});
            skLineSegment(sketch, "E65.MirrorCS", {"start": v(-239.62, 10.6) * mm, "end": v(-239.73, 5.6) * mm});
            skLineSegment(sketch, "E66.MirrorCS", {"start": v(-337.5, 45.6) * mm, "end": v(-333.23, 43) * mm});
            skLineSegment(sketch, "E67.MirrorCS", {"start": v(-347.69, -36.98) * mm, "end": v(-343.3, -34.58) * mm});
            skLineSegment(sketch, "E68.MirrorCS", {"start": v(-253.39, 50.6) * mm, "end": v(-253.5, 45.6) * mm});
            skLineSegment(sketch, "E69.MirrorCS", {"start": v(-347.23, 13) * mm, "end": v(-351.62, 10.6) * mm});
            skLineSegment(sketch, "E70.MirrorCS", {"start": v(-272.61, 70.4) * mm, "end": v(-276.89, 73) * mm});
            skLineSegment(sketch, "E71.MirrorCS", {"start": v(-333.57, -16.99) * mm, "end": v(-329.19, -14.59) * mm});
            skLineSegment(sketch, "E72.MirrorCS", {"start": v(-314.96, 10.4) * mm, "end": v(-319.23, 13) * mm});
            skLineSegment(sketch, "E73.MirrorCS", {"start": v(-337.39, 50.6) * mm, "end": v(-337.5, 45.6) * mm});
            skLineSegment(sketch, "E74.MirrorCS", {"start": v(-343.19, -29.59) * mm, "end": v(-347.46, -26.99) * mm});
            skLineSegment(sketch, "E75.MirrorCS", {"start": v(-253.73, -9.4) * mm, "end": v(-253.84, -14.4) * mm});
            skLineSegment(sketch, "E76.MirrorCS", {"start": v(-230.73, 50.4) * mm, "end": v(-235, 53) * mm});
            skLineSegment(sketch, "E77.MirrorCS", {"start": v(-315.3, -49.59) * mm, "end": v(-319.57, -46.99) * mm});
            skLineSegment(sketch, "E78.MirrorCS", {"start": v(-249.57, -47) * mm, "end": v(-253.96, -49.4) * mm});
            skLineSegment(sketch, "E79.MirrorCS", {"start": v(-234.89, 73) * mm, "end": v(-248.89, 73) * mm, "construction": true});
            skLineSegment(sketch, "E80.MirrorCS", {"start": v(-267.5, 30.6) * mm, "end": v(-267.62, 25.6) * mm});
            skLineSegment(sketch, "E81.MirrorCS", {"start": v(-346.89, 73) * mm, "end": v(-351.27, 70.6) * mm});
            skLineSegment(sketch, "E82.MirrorCS", {"start": v(-291.23, 43) * mm, "end": v(-286.84, 45.4) * mm});
            skLineSegment(sketch, "E83.MirrorCS", {"start": v(-234.89, 73) * mm, "end": v(-235, 53) * mm, "construction": true});
            skLineSegment(sketch, "E84.MirrorCS", {"start": v(-329.19, -14.59) * mm, "end": v(-329.07, -9.59) * mm});
            skLineSegment(sketch, "E85.MirrorCS", {"start": v(-253.39, 65.6) * mm, "end": v(-249.11, 63) * mm});
            skLineSegment(sketch, "E86.MirrorCS", {"start": v(-244.73, 65.4) * mm, "end": v(-244.61, 70.4) * mm});
            skLineSegment(sketch, "E87.MirrorCS", {"start": v(-295.73, -9.4) * mm, "end": v(-295.84, -14.4) * mm});
            skLineSegment(sketch, "E88.MirrorCS", {"start": v(-248.89, 73) * mm, "end": v(-253.27, 70.6) * mm});
            skLineSegment(sketch, "E89.MirrorCS", {"start": v(-351.84, -29.39) * mm, "end": v(-351.96, -34.39) * mm});
            skLineSegment(sketch, "E90.MirrorCS", {"start": v(-263.11, 63) * mm, "end": v(-258.73, 65.4) * mm});
            skLineSegment(sketch, "E91.MirrorCS", {"start": v(-295.5, 45.6) * mm, "end": v(-291.23, 43) * mm});
            skLineSegment(sketch, "E92.MirrorCS", {"start": v(-281.96, -49.4) * mm, "end": v(-282.07, -54.39) * mm});
            skLineSegment(sketch, "E93.MirrorCS", {"start": v(-244.73, 50.4) * mm, "end": v(-249, 53) * mm});
            skLineSegment(sketch, "E94.MirrorCS", {"start": v(-281.39, 65.6) * mm, "end": v(-277.11, 63) * mm});
            skLineSegment(sketch, "E95.MirrorCS", {"start": v(-309.84, -29.4) * mm, "end": v(-309.96, -34.39) * mm});
            skLineSegment(sketch, "E96.MirrorCS", {"start": v(-277.57, -47) * mm, "end": v(-281.96, -49.4) * mm});
            skLineSegment(sketch, "E97.MirrorCS", {"start": v(-277.11, 63) * mm, "end": v(-272.73, 65.4) * mm});
            skLineSegment(sketch, "E98.MirrorCS", {"start": v(-245.3, -49.6) * mm, "end": v(-249.57, -47) * mm});
            skLineSegment(sketch, "E99.MirrorCS", {"start": v(-253.27, 70.6) * mm, "end": v(-253.39, 65.6) * mm});
            skLineSegment(sketch, "E100.MirrorCS", {"start": v(-329.07, -9.59) * mm, "end": v(-333.34, -6.99) * mm});
            skLineSegment(sketch, "E101.MirrorCS", {"start": v(-300.84, 30.4) * mm, "end": v(-305.11, 33) * mm});
            skLineSegment(sketch, "E102.MirrorCS", {"start": v(-286.73, 50.4) * mm, "end": v(-291, 53) * mm});
            skLineSegment(sketch, "E103.MirrorCS", {"start": v(-286.84, 45.4) * mm, "end": v(-286.73, 50.4) * mm});
            skLineSegment(sketch, "E104.MirrorCS", {"start": v(-333.23, 43) * mm, "end": v(-328.84, 45.4) * mm});
            skLineSegment(sketch, "E105.MirrorCS", {"start": v(-337.5, 30.6) * mm, "end": v(-337.62, 25.6) * mm});
            skLineSegment(sketch, "E106.MirrorCS", {"start": v(-328.84, 45.4) * mm, "end": v(-328.73, 50.4) * mm});
            skLineSegment(sketch, "E107.MirrorCS", {"start": v(-304.89, 73) * mm, "end": v(-309.27, 70.6) * mm});
            skLineSegment(sketch, "E108.MirrorCS", {"start": v(-323.96, -49.39) * mm, "end": v(-324.07, -54.39) * mm});
            skLineSegment(sketch, "E109.MirrorCS", {"start": v(-314.73, 65.4) * mm, "end": v(-314.61, 70.4) * mm});
            skLineSegment(sketch, "E110.MirrorCS", {"start": v(-249.8, -56.99) * mm, "end": v(-245.41, -54.59) * mm});
            skLineSegment(sketch, "E111.MirrorCS", {"start": v(-267.39, 65.6) * mm, "end": v(-263.11, 63) * mm});
            skLineSegment(sketch, "E112.MirrorCS", {"start": v(-315.07, 5.41) * mm, "end": v(-314.96, 10.4) * mm});
            skLineSegment(sketch, "E113.MirrorCS", {"start": v(-259.19, -14.6) * mm, "end": v(-259.07, -9.6) * mm});
            skCircle(sketch, "E114.MirrorC", {"center": v(-235, 68) * mm, "radius": 4.33 * mm, "construction": true});
            skLineSegment(sketch, "E115.MirrorCS", {"start": v(-351.27, 70.6) * mm, "end": v(-351.39, 65.6) * mm});
            skLineSegment(sketch, "E116.MirrorCS", {"start": v(-309.27, 70.6) * mm, "end": v(-309.39, 65.6) * mm});
            skLineSegment(sketch, "E117.MirrorCS", {"start": v(-263.11, 33) * mm, "end": v(-267.5, 30.6) * mm});
            skLineSegment(sketch, "E118.MirrorCS", {"start": v(-300.96, 25.4) * mm, "end": v(-300.84, 30.4) * mm});
            skLineSegment(sketch, "E119.MirrorCS", {"start": v(-351.62, 10.6) * mm, "end": v(-351.73, 5.61) * mm});
            skLineSegment(sketch, "E120.MirrorCS", {"start": v(-295.5, 30.6) * mm, "end": v(-295.62, 25.6) * mm});
            skLineSegment(sketch, "E121.MirrorCS", {"start": v(-287.41, -54.59) * mm, "end": v(-287.3, -49.59) * mm});
            skLineSegment(sketch, "E122.MirrorCS", {"start": v(-263.46, -27) * mm, "end": v(-267.84, -29.4) * mm});
            skLineSegment(sketch, "E123.MirrorCS", {"start": v(-337.73, -9.39) * mm, "end": v(-337.84, -14.39) * mm});
            skLineSegment(sketch, "E124.MirrorCS", {"start": v(-323.62, 25.6) * mm, "end": v(-319.34, 23) * mm});
            skLineSegment(sketch, "E125.MirrorCS", {"start": v(-263.34, 23) * mm, "end": v(-258.96, 25.4) * mm});
            skLineSegment(sketch, "E126.MirrorCS", {"start": v(-249.23, 43) * mm, "end": v(-244.84, 45.4) * mm});
            skLineSegment(sketch, "E127.MirrorCS", {"start": v(-300.73, 65.4) * mm, "end": v(-300.61, 70.4) * mm});
            skLineSegment(sketch, "E128.MirrorCS", {"start": v(-333.46, 3.01) * mm, "end": v(-329.07, 5.41) * mm});
            skLineSegment(sketch, "E129.MirrorCS", {"start": v(-328.96, 10.41) * mm, "end": v(-333.23, 13) * mm});
            skLineSegment(sketch, "E130.MirrorCS", {"start": v(-258.73, 65.4) * mm, "end": v(-258.61, 70.4) * mm});
            skLineSegment(sketch, "E131.MirrorCS", {"start": v(-305.46, 3) * mm, "end": v(-301.07, 5.41) * mm});
            skLineSegment(sketch, "E132.MirrorCS", {"start": v(-253.62, 25.6) * mm, "end": v(-249.34, 23) * mm});
            skLineSegment(sketch, "E133.MirrorCS", {"start": v(-245.07, -9.6) * mm, "end": v(-249.34, -7) * mm});
            skLineSegment(sketch, "E134.MirrorCS", {"start": v(-315.3, -34.59) * mm, "end": v(-315.19, -29.59) * mm});
            skLineSegment(sketch, "E135.MirrorCS", {"start": v(-337.84, -29.39) * mm, "end": v(-337.96, -34.39) * mm});
            skLineSegment(sketch, "E136.MirrorCS", {"start": v(-239.84, -29.4) * mm, "end": v(-239.96, -34.4) * mm});
            skLineSegment(sketch, "E137.MirrorCS", {"start": v(-319.8, -56.99) * mm, "end": v(-315.41, -54.59) * mm});
            skLineSegment(sketch, "E138.MirrorCS", {"start": v(-287.19, -14.59) * mm, "end": v(-287.07, -9.6) * mm});
            skLineSegment(sketch, "E139.MirrorCS", {"start": v(-258.61, 70.4) * mm, "end": v(-262.89, 73) * mm});
            skLineSegment(sketch, "E140.MirrorCS", {"start": v(-319.46, 3.01) * mm, "end": v(-315.07, 5.41) * mm});
            skLineSegment(sketch, "E141.MirrorCS", {"start": v(-273.07, -9.6) * mm, "end": v(-277.34, -7) * mm});
            skLineSegment(sketch, "E142.MirrorCS", {"start": v(-230.84, 45.4) * mm, "end": v(-230.73, 50.4) * mm});
            skLineSegment(sketch, "E143.MirrorCS", {"start": v(-333.46, -26.99) * mm, "end": v(-337.84, -29.39) * mm});
            skLineSegment(sketch, "E144.MirrorCS", {"start": v(-347.23, 43) * mm, "end": v(-342.84, 45.41) * mm});
            skLineSegment(sketch, "E145.MirrorCS", {"start": v(-267.39, 50.6) * mm, "end": v(-267.5, 45.6) * mm});
            skLineSegment(sketch, "E146.MirrorCS", {"start": v(-277.46, 3) * mm, "end": v(-273.07, 5.4) * mm});
            skLineSegment(sketch, "E147.MirrorCS", {"start": v(-277.69, -36.99) * mm, "end": v(-273.3, -34.59) * mm});
            skLineSegment(sketch, "E148.MirrorCS", {"start": v(-263.8, -56.99) * mm, "end": v(-259.41, -54.59) * mm});
            skLineSegment(sketch, "E149.MirrorCS", {"start": v(-259.3, -34.6) * mm, "end": v(-259.19, -29.6) * mm});
            skLineSegment(sketch, "E150.MirrorCS", {"start": v(-253.62, 10.6) * mm, "end": v(-253.73, 5.6) * mm});
            skLineSegment(sketch, "E151.MirrorCS", {"start": v(-267.73, 5.6) * mm, "end": v(-263.46, 3) * mm});
            skLineSegment(sketch, "E152.MirrorCS", {"start": v(-300.73, 50.4) * mm, "end": v(-305, 53) * mm});
            skLineSegment(sketch, "E153.MirrorCS", {"start": v(-281.84, -29.4) * mm, "end": v(-281.96, -34.4) * mm});
            skLineSegment(sketch, "E154.MirrorCS", {"start": v(-281.5, 30.6) * mm, "end": v(-281.62, 25.6) * mm});
            skLineSegment(sketch, "E155.MirrorCS", {"start": v(-347.8, -56.98) * mm, "end": v(-343.41, -54.58) * mm});
            skLineSegment(sketch, "E156.MirrorCS", {"start": v(-291.23, 13) * mm, "end": v(-295.62, 10.6) * mm});
            skLineSegment(sketch, "E157.MirrorCS", {"start": v(-305.11, 33) * mm, "end": v(-309.5, 30.6) * mm});
            skLineSegment(sketch, "E158.MirrorCS", {"start": v(-315.19, -14.59) * mm, "end": v(-315.07, -9.59) * mm});
            skLineSegment(sketch, "E159.MirrorCS", {"start": v(-263.23, 13) * mm, "end": v(-267.62, 10.6) * mm});
            skLineSegment(sketch, "E160.MirrorCS", {"start": v(-323.5, 45.6) * mm, "end": v(-319.23, 43) * mm});
            skLineSegment(sketch, "E161.MirrorCS", {"start": v(-301.3, -34.59) * mm, "end": v(-301.19, -29.59) * mm});
            skLineSegment(sketch, "E162.MirrorCS", {"start": v(-347.46, -26.99) * mm, "end": v(-351.84, -29.39) * mm});
            skLineSegment(sketch, "E163.MirrorCS", {"start": v(-309.96, -34.39) * mm, "end": v(-305.69, -36.99) * mm});
            skLineSegment(sketch, "E164.MirrorCS", {"start": v(-239.39, 50.6) * mm, "end": v(-239.5, 45.6) * mm});
            skLineSegment(sketch, "E165.MirrorCS", {"start": v(-259.07, -9.6) * mm, "end": v(-263.34, -7) * mm});
            skLineSegment(sketch, "E166.MirrorCS", {"start": v(-309.62, 25.6) * mm, "end": v(-305.34, 23) * mm});
            skLineSegment(sketch, "E167.MirrorCS", {"start": v(-314.84, 30.4) * mm, "end": v(-319.11, 33) * mm});
            skLineSegment(sketch, "E168.MirrorCS", {"start": v(-281.84, -14.4) * mm, "end": v(-277.57, -17) * mm});
            skLineSegment(sketch, "E169.MirrorCS", {"start": v(-323.5, 30.6) * mm, "end": v(-323.62, 25.6) * mm});
            skLineSegment(sketch, "E170.MirrorCS", {"start": v(-291.57, -46.99) * mm, "end": v(-295.96, -49.4) * mm});
            skLineSegment(sketch, "E171.MirrorCS", {"start": v(-333, 53) * mm, "end": v(-337.39, 50.6) * mm});
            skLineSegment(sketch, "E172.MirrorCS", {"start": v(-295.39, 65.6) * mm, "end": v(-291.11, 63) * mm});
            skLineSegment(sketch, "E173.MirrorCS", {"start": v(-347.57, -46.99) * mm, "end": v(-351.96, -49.39) * mm});
            skLineSegment(sketch, "E174.MirrorCS", {"start": v(-319.34, -7) * mm, "end": v(-323.73, -9.4) * mm});
            skLineSegment(sketch, "E175.MirrorCS", {"start": v(-309.84, -14.4) * mm, "end": v(-305.57, -16.99) * mm});
            skLineSegment(sketch, "E176.MirrorCS", {"start": v(-273.3, -34.59) * mm, "end": v(-273.19, -29.6) * mm});
            skLineSegment(sketch, "E177.MirrorCS", {"start": v(-277.11, 33) * mm, "end": v(-281.5, 30.6) * mm});
            skLineSegment(sketch, "E178.MirrorCS", {"start": v(-333.57, -46.99) * mm, "end": v(-337.96, -49.39) * mm});
            skLineSegment(sketch, "E179.MirrorCS", {"start": v(-347.11, 63) * mm, "end": v(-342.73, 65.4) * mm});
            skLineSegment(sketch, "E180.MirrorCS", {"start": v(-309.62, 10.6) * mm, "end": v(-309.73, 5.6) * mm});
            skLineSegment(sketch, "E181.MirrorCS", {"start": v(-309.39, 50.6) * mm, "end": v(-309.5, 45.6) * mm});
            skLineSegment(sketch, "E182.MirrorCS", {"start": v(-231.19, -29.6) * mm, "end": v(-235.46, -27) * mm});
            skLineSegment(sketch, "E183.MirrorCS", {"start": v(-239.73, 5.6) * mm, "end": v(-235.46, 3) * mm});
            skLineSegment(sketch, "E184.MirrorCS", {"start": v(-235.34, -7) * mm, "end": v(-239.73, -9.4) * mm});
            skLineSegment(sketch, "E185.MirrorCS", {"start": v(-272.96, 25.4) * mm, "end": v(-272.84, 30.4) * mm});
            skLineSegment(sketch, "E186.MirrorCS", {"start": v(-328.96, 25.41) * mm, "end": v(-328.84, 30.4) * mm});
            skLineSegment(sketch, "E187.MirrorCS", {"start": v(-268.07, -54.4) * mm, "end": v(-263.8, -56.99) * mm});
            skLineSegment(sketch, "E188.MirrorCS", {"start": v(-235.34, 23) * mm, "end": v(-230.96, 25.4) * mm});
            skLineSegment(sketch, "E189.MirrorCS", {"start": v(-309.73, -9.4) * mm, "end": v(-309.84, -14.4) * mm});
            skLineSegment(sketch, "E190.MirrorCS", {"start": v(-309.5, 45.6) * mm, "end": v(-305.23, 43) * mm});
            skLineSegment(sketch, "E191.MirrorCS", {"start": v(-235.57, -17) * mm, "end": v(-231.19, -14.6) * mm});
            skLineSegment(sketch, "E192.MirrorCS", {"start": v(-287.07, 5.4) * mm, "end": v(-286.96, 10.4) * mm});
            skLineSegment(sketch, "E193.MirrorCS", {"start": v(-301.07, 5.41) * mm, "end": v(-300.96, 10.4) * mm});
            skLineSegment(sketch, "E194.MirrorCS", {"start": v(-276.89, 73) * mm, "end": v(-281.27, 70.6) * mm});
            skLineSegment(sketch, "E195.MirrorCS", {"start": v(-351.5, 45.6) * mm, "end": v(-347.23, 43) * mm});
            skLineSegment(sketch, "E196.MirrorCS", {"start": v(-231.07, 5.4) * mm, "end": v(-230.96, 10.4) * mm});
            skLineSegment(sketch, "E197.MirrorCS", {"start": v(-273.3, -49.59) * mm, "end": v(-277.57, -47) * mm});
            skLineSegment(sketch, "E198.MirrorCS", {"start": v(-305.23, 43) * mm, "end": v(-300.84, 45.4) * mm});
            skLineSegment(sketch, "E199.MirrorCS", {"start": v(-235.46, -27) * mm, "end": v(-239.84, -29.4) * mm});
            skLineSegment(sketch, "E200.MirrorCS", {"start": v(-272.84, 30.4) * mm, "end": v(-277.11, 33) * mm});
            skLineSegment(sketch, "E201.MirrorCS", {"start": v(-263.57, -47) * mm, "end": v(-267.96, -49.4) * mm});
            skLineSegment(sketch, "E202.MirrorCS", {"start": v(-277.34, -7) * mm, "end": v(-281.73, -9.4) * mm});
            skLineSegment(sketch, "E203.MirrorCS", {"start": v(-239.96, -34.4) * mm, "end": v(-235.69, -37) * mm});
            skLineSegment(sketch, "E204.MirrorCS", {"start": v(-337.39, 65.6) * mm, "end": v(-333.11, 63) * mm});
            skLineSegment(sketch, "E205.MirrorCS", {"start": v(-230.73, 65.4) * mm, "end": v(-230.61, 70.4) * mm});
            skLineSegment(sketch, "E206.MirrorCS", {"start": v(-249.11, 33) * mm, "end": v(-253.5, 30.6) * mm});
            skLineSegment(sketch, "E207.MirrorCS", {"start": v(-347.34, -6.99) * mm, "end": v(-351.73, -9.39) * mm});
            skLineSegment(sketch, "E208.MirrorCS", {"start": v(-259.41, -54.59) * mm, "end": v(-259.3, -49.6) * mm});
            skLineSegment(sketch, "E209.MirrorCS", {"start": v(-235.8, -57) * mm, "end": v(-231.41, -54.6) * mm});
            skLineSegment(sketch, "E210.MirrorCS", {"start": v(-230.84, 30.4) * mm, "end": v(-235.11, 33) * mm});
            skLineSegment(sketch, "E211.MirrorCS", {"start": v(-263.46, 3) * mm, "end": v(-259.07, 5.4) * mm});
            skLineSegment(sketch, "E212.MirrorCS", {"start": v(-239.5, 30.6) * mm, "end": v(-239.62, 25.6) * mm});
            skLineSegment(sketch, "E213.MirrorCS", {"start": v(-319.11, 33) * mm, "end": v(-323.5, 30.6) * mm});
            skLineSegment(sketch, "E214.MirrorCS", {"start": v(-245.3, -34.6) * mm, "end": v(-245.19, -29.6) * mm});
            skLineSegment(sketch, "E215.MirrorCS", {"start": v(-351.39, 65.6) * mm, "end": v(-347.11, 63) * mm});
            skLineSegment(sketch, "E216.MirrorCS", {"start": v(-258.84, 30.4) * mm, "end": v(-263.11, 33) * mm});
            skLineSegment(sketch, "E217.MirrorCS", {"start": v(-239.96, -49.4) * mm, "end": v(-240.07, -54.4) * mm});
            skLineSegment(sketch, "E218.MirrorCS", {"start": v(-277.57, -17) * mm, "end": v(-273.19, -14.6) * mm});
            skLineSegment(sketch, "E219.MirrorCS", {"start": v(-291.11, 33) * mm, "end": v(-295.5, 30.6) * mm});
            skLineSegment(sketch, "E220.MirrorCS", {"start": v(-305.23, 13) * mm, "end": v(-309.62, 10.6) * mm});
            skLineSegment(sketch, "E221.MirrorCS", {"start": v(-329.41, -54.58) * mm, "end": v(-329.3, -49.59) * mm});
            skLineSegment(sketch, "E222.MirrorCS", {"start": v(-305.57, -16.99) * mm, "end": v(-301.19, -14.59) * mm});
            skLineSegment(sketch, "E223.MirrorCS", {"start": v(-319.34, 23) * mm, "end": v(-314.96, 25.4) * mm});
            skLineSegment(sketch, "E224.MirrorCS", {"start": v(-244.96, 10.4) * mm, "end": v(-249.23, 13) * mm});
            skLineSegment(sketch, "E225.MirrorCS", {"start": v(-324.07, -54.39) * mm, "end": v(-319.8, -56.99) * mm});
            skLineSegment(sketch, "E226.MirrorCS", {"start": v(-328.73, 65.4) * mm, "end": v(-328.61, 70.4) * mm});
            skLineSegment(sketch, "E227.MirrorCS", {"start": v(-323.84, -14.39) * mm, "end": v(-319.57, -16.99) * mm});
            skLineSegment(sketch, "E228.MirrorCS", {"start": v(-235.23, 43) * mm, "end": v(-230.84, 45.4) * mm});
            skLineSegment(sketch, "E229.MirrorCS", {"start": v(-262.89, 73) * mm, "end": v(-267.27, 70.6) * mm});
            skLineSegment(sketch, "E230.MirrorCS", {"start": v(-287.3, -49.59) * mm, "end": v(-291.57, -46.99) * mm});
            skLineSegment(sketch, "E231.MirrorCS", {"start": v(-295.96, -49.4) * mm, "end": v(-296.07, -54.39) * mm});
            skLineSegment(sketch, "E232.MirrorCS", {"start": v(-351.84, -14.39) * mm, "end": v(-347.57, -16.99) * mm});
            skLineSegment(sketch, "E233.MirrorCS", {"start": v(-281.62, 25.6) * mm, "end": v(-277.34, 23) * mm});
            skLineSegment(sketch, "E234.MirrorCS", {"start": v(-277.34, 23) * mm, "end": v(-272.96, 25.4) * mm});
            skLineSegment(sketch, "E235.MirrorCS", {"start": v(-315.07, -9.59) * mm, "end": v(-319.34, -7) * mm});
            skLineSegment(sketch, "E236.MirrorCS", {"start": v(-249.34, 23) * mm, "end": v(-244.96, 25.4) * mm});
            skLineSegment(sketch, "E237.MirrorCS", {"start": v(-342.96, 10.41) * mm, "end": v(-347.23, 13) * mm});
            skLineSegment(sketch, "E238.MirrorCS", {"start": v(-342.73, 50.4) * mm, "end": v(-347, 53) * mm});
            skLineSegment(sketch, "E239.MirrorCS", {"start": v(-333.69, -36.99) * mm, "end": v(-329.3, -34.59) * mm});
            skLineSegment(sketch, "E240.MirrorCS", {"start": v(-263.34, -7) * mm, "end": v(-267.73, -9.4) * mm});
            skLineSegment(sketch, "E241.MirrorCS", {"start": v(-319.69, -36.99) * mm, "end": v(-315.3, -34.59) * mm});
            skLineSegment(sketch, "E242.MirrorCS", {"start": v(-310.07, -54.39) * mm, "end": v(-305.8, -56.99) * mm});
            skLineSegment(sketch, "E243.MirrorCS", {"start": v(-318.89, 73) * mm, "end": v(-323.27, 70.6) * mm});
            skLineSegment(sketch, "E244.MirrorCS", {"start": v(-286.96, 10.4) * mm, "end": v(-291.23, 13) * mm});
            skLineSegment(sketch, "E245.MirrorCS", {"start": v(-347.34, 23.01) * mm, "end": v(-342.96, 25.41) * mm});
            skLineSegment(sketch, "E246.MirrorCS", {"start": v(-301.19, -14.59) * mm, "end": v(-301.07, -9.59) * mm});
            skLineSegment(sketch, "E247.MirrorCS", {"start": v(-305.69, -36.99) * mm, "end": v(-301.3, -34.59) * mm});
            skLineSegment(sketch, "E248.MirrorCS", {"start": v(-319.46, -26.99) * mm, "end": v(-323.84, -29.39) * mm});
            skLineSegment(sketch, "E249.MirrorCS", {"start": v(-314.96, 25.4) * mm, "end": v(-314.84, 30.4) * mm});
            skLineSegment(sketch, "E250.MirrorCS", {"start": v(-347, 53) * mm, "end": v(-351.39, 50.6) * mm});
            skLineSegment(sketch, "E251.MirrorCS", {"start": v(-342.61, 70.4) * mm, "end": v(-346.89, 73) * mm});
            skLineSegment(sketch, "E252.MirrorCS", {"start": v(-295.27, 70.6) * mm, "end": v(-295.39, 65.6) * mm});
            skLineSegment(sketch, "E253.MirrorCS", {"start": v(-244.84, 30.4) * mm, "end": v(-249.11, 33) * mm});
            skLineSegment(sketch, "E254.MirrorCS", {"start": v(-259.19, -29.6) * mm, "end": v(-263.46, -27) * mm});
            skLineSegment(sketch, "E255.MirrorCS", {"start": v(-329.07, 5.41) * mm, "end": v(-328.96, 10.41) * mm});
            skLineSegment(sketch, "E256.MirrorCS", {"start": v(-272.84, 45.4) * mm, "end": v(-272.73, 50.4) * mm});
            skLineSegment(sketch, "E257.MirrorCS", {"start": v(-267.96, -34.4) * mm, "end": v(-263.69, -37) * mm});
            skLineSegment(sketch, "E258.MirrorCS", {"start": v(-231.19, -14.6) * mm, "end": v(-231.07, -9.6) * mm});
            skLineSegment(sketch, "E259.MirrorCS", {"start": v(-281.73, -9.4) * mm, "end": v(-281.84, -14.4) * mm});
            skLineSegment(sketch, "E260.MirrorCS", {"start": v(-249.69, -37) * mm, "end": v(-245.3, -34.6) * mm});
            skLineSegment(sketch, "E261.MirrorCS", {"start": v(-277.46, -27) * mm, "end": v(-281.84, -29.4) * mm});
            skLineSegment(sketch, "E262.MirrorCS", {"start": v(-329.3, -49.59) * mm, "end": v(-333.57, -46.99) * mm});
            skLineSegment(sketch, "E263.MirrorCS", {"start": v(-230.96, 10.4) * mm, "end": v(-235.23, 13) * mm});
            skLineSegment(sketch, "E264.MirrorCS", {"start": v(-286.96, 25.4) * mm, "end": v(-286.84, 30.4) * mm});
            skLineSegment(sketch, "E265.MirrorCS", {"start": v(-342.73, 65.4) * mm, "end": v(-342.61, 70.4) * mm});
            skLineSegment(sketch, "E266.MirrorCS", {"start": v(-230.96, 25.4) * mm, "end": v(-230.84, 30.4) * mm});
            skLineSegment(sketch, "E267.MirrorCS", {"start": v(-277, 53) * mm, "end": v(-281.39, 50.6) * mm});
            skLineSegment(sketch, "E268.MirrorCS", {"start": v(-305.34, -7) * mm, "end": v(-309.73, -9.4) * mm});
            skLineSegment(sketch, "E269.MirrorCS", {"start": v(-295.96, -34.4) * mm, "end": v(-291.69, -36.99) * mm});
            skLineSegment(sketch, "E270.MirrorCS", {"start": v(-342.84, 45.41) * mm, "end": v(-342.73, 50.4) * mm});
            skLineSegment(sketch, "E271.MirrorCS", {"start": v(-314.73, 50.4) * mm, "end": v(-319, 53) * mm});
            skLineSegment(sketch, "E272.MirrorCS", {"start": v(-343.07, -9.59) * mm, "end": v(-347.34, -6.99) * mm});
            skLineSegment(sketch, "E273.MirrorCS", {"start": v(-286.73, 65.4) * mm, "end": v(-286.61, 70.4) * mm});
            skLineSegment(sketch, "E274.MirrorCS", {"start": v(-337.62, 10.6) * mm, "end": v(-337.73, 5.61) * mm});
            skLineSegment(sketch, "E275.MirrorCS", {"start": v(-282.07, -54.39) * mm, "end": v(-277.8, -56.99) * mm});
            skLineSegment(sketch, "E276.MirrorCS", {"start": v(-333.34, 23.01) * mm, "end": v(-328.96, 25.41) * mm});
            skLineSegment(sketch, "E277.MirrorCS", {"start": v(-347.57, -16.99) * mm, "end": v(-343.19, -14.59) * mm});
            skLineSegment(sketch, "E278.MirrorCS", {"start": v(-291.11, 63) * mm, "end": v(-286.73, 65.4) * mm});
            skLineSegment(sketch, "E279.MirrorCS", {"start": v(-319.57, -16.99) * mm, "end": v(-315.19, -14.59) * mm});
            skLineSegment(sketch, "E280.MirrorCS", {"start": v(-323.62, 10.6) * mm, "end": v(-323.73, 5.6) * mm});
            skLineSegment(sketch, "E281.MirrorCS", {"start": v(-267.96, -49.4) * mm, "end": v(-268.07, -54.4) * mm});
            skLineSegment(sketch, "E282.MirrorCS", {"start": v(-249.23, 13) * mm, "end": v(-253.62, 10.6) * mm});
            skLineSegment(sketch, "E283.MirrorCS", {"start": v(-287.19, -29.59) * mm, "end": v(-291.46, -27) * mm});
            skLineSegment(sketch, "E284.MirrorCS", {"start": v(-281.5, 45.6) * mm, "end": v(-277.23, 43) * mm});
            skLineSegment(sketch, "E285.MirrorCS", {"start": v(-319.11, 63) * mm, "end": v(-314.73, 65.4) * mm});
            skLineSegment(sketch, "E286.MirrorCS", {"start": v(-295.62, 25.6) * mm, "end": v(-291.34, 23) * mm});
            skLineSegment(sketch, "E287.MirrorCS", {"start": v(-337.96, -34.39) * mm, "end": v(-333.69, -36.99) * mm});
            skLineSegment(sketch, "E288.MirrorCS", {"start": v(-315.19, -29.59) * mm, "end": v(-319.46, -26.99) * mm});
            skLineSegment(sketch, "E289.MirrorCS", {"start": v(-300.84, 45.4) * mm, "end": v(-300.73, 50.4) * mm});
            skLineSegment(sketch, "E290.MirrorCS", {"start": v(-351.5, 30.6) * mm, "end": v(-351.62, 25.6) * mm});
            skLineSegment(sketch, "E291.MirrorCS", {"start": v(-290.89, 73) * mm, "end": v(-295.27, 70.6) * mm});
            skLineSegment(sketch, "E292.MirrorCS", {"start": v(-235.57, -47) * mm, "end": v(-239.96, -49.4) * mm});
            skLineSegment(sketch, "E293.MirrorCS", {"start": v(-337.27, 70.6) * mm, "end": v(-337.39, 65.6) * mm});
            skLineSegment(sketch, "E294.MirrorCS", {"start": v(-259.3, -49.6) * mm, "end": v(-263.57, -47) * mm});
            skLineSegment(sketch, "E295.MirrorCS", {"start": v(-343.41, -54.58) * mm, "end": v(-343.3, -49.58) * mm});
            skLineSegment(sketch, "E296.MirrorCS", {"start": v(-286.61, 70.4) * mm, "end": v(-290.89, 73) * mm});
            skLineSegment(sketch, "E297.MirrorCS", {"start": v(-333.11, 63) * mm, "end": v(-328.73, 65.4) * mm});
            skLineSegment(sketch, "E298.MirrorCS", {"start": v(-249.57, -17) * mm, "end": v(-245.19, -14.6) * mm});
            skLineSegment(sketch, "E299.MirrorCS", {"start": v(-295.73, 5.6) * mm, "end": v(-291.46, 3) * mm});
            skLineSegment(sketch, "E300.MirrorCS", {"start": v(-231.07, -9.6) * mm, "end": v(-235.34, -7) * mm});
            skLineSegment(sketch, "E301.MirrorCS", {"start": v(-272.73, 50.4) * mm, "end": v(-277, 53) * mm});
            skLineSegment(sketch, "E302.MirrorCS", {"start": v(-239.84, -14.4) * mm, "end": v(-235.57, -17) * mm});
            skLineSegment(sketch, "E303.MirrorCS", {"start": v(-351.96, -34.39) * mm, "end": v(-347.69, -36.98) * mm});
            skLineSegment(sketch, "E304.MirrorCS", {"start": v(-239.73, -9.4) * mm, "end": v(-239.84, -14.4) * mm});
            skLineSegment(sketch, "E305.MirrorCS", {"start": v(-235.11, 33) * mm, "end": v(-239.5, 30.6) * mm});
            skLineSegment(sketch, "E306.MirrorCS", {"start": v(-231.3, -34.6) * mm, "end": v(-231.19, -29.6) * mm});
            skLineSegment(sketch, "E307.MirrorCS", {"start": v(-267.62, 10.6) * mm, "end": v(-267.73, 5.6) * mm});
            skLineSegment(sketch, "E308.MirrorCS", {"start": v(-277.8, -56.99) * mm, "end": v(-273.41, -54.59) * mm});
            skLineSegment(sketch, "E309.MirrorCS", {"start": v(-291.46, 3) * mm, "end": v(-287.07, 5.4) * mm});
            skLineSegment(sketch, "E310.MirrorCS", {"start": v(-351.62, 25.6) * mm, "end": v(-347.34, 23.01) * mm});
            skLineSegment(sketch, "E311.MirrorCS", {"start": v(-323.39, 65.6) * mm, "end": v(-319.11, 63) * mm});
            skLineSegment(sketch, "E312.MirrorCS", {"start": v(-309.39, 65.6) * mm, "end": v(-305.11, 63) * mm});
            skLineSegment(sketch, "E313.MirrorCS", {"start": v(-323.73, -9.4) * mm, "end": v(-323.84, -14.39) * mm});
            skLineSegment(sketch, "E314.MirrorCS", {"start": v(-295.84, -29.4) * mm, "end": v(-295.96, -34.4) * mm});
            skLineSegment(sketch, "E315.MirrorCS", {"start": v(-273.07, 5.4) * mm, "end": v(-272.96, 10.4) * mm});
            skLineSegment(sketch, "E316.MirrorCS", {"start": v(-337.73, 5.61) * mm, "end": v(-333.46, 3.01) * mm});
            skLineSegment(sketch, "E317.MirrorCS", {"start": v(-253.5, 45.6) * mm, "end": v(-249.23, 43) * mm});
            skLineSegment(sketch, "E318.MirrorCS", {"start": v(-291.57, -16.99) * mm, "end": v(-287.19, -14.59) * mm});
            skLineSegment(sketch, "E319.MirrorCS", {"start": v(-296.07, -54.39) * mm, "end": v(-291.8, -56.99) * mm});
            skLineSegment(sketch, "E320.MirrorCS", {"start": v(-351.39, 50.6) * mm, "end": v(-351.5, 45.6) * mm});
            skLineSegment(sketch, "E321.MirrorCS", {"start": v(-258.73, 50.4) * mm, "end": v(-263, 53) * mm});
            skLineSegment(sketch, "E322.MirrorCS", {"start": v(-333.23, 13) * mm, "end": v(-337.62, 10.6) * mm});
            skLineSegment(sketch, "E323.MirrorCS", {"start": v(-301.07, -9.59) * mm, "end": v(-305.34, -7) * mm});
            skLineSegment(sketch, "E324.MirrorCS", {"start": v(-343.19, -14.59) * mm, "end": v(-343.07, -9.59) * mm});
            skLineSegment(sketch, "E325.MirrorCS", {"start": v(-319.23, 13) * mm, "end": v(-323.62, 10.6) * mm});
            skLineSegment(sketch, "E326.MirrorCS", {"start": v(-231.41, -54.6) * mm, "end": v(-231.3, -49.6) * mm});
            skLineSegment(sketch, "E327.MirrorCS", {"start": v(-314.84, 45.4) * mm, "end": v(-314.73, 50.4) * mm});
            skLineSegment(sketch, "E328.MirrorCS", {"start": v(-281.96, -34.4) * mm, "end": v(-277.69, -36.99) * mm});
            skLineSegment(sketch, "E329.MirrorCS", {"start": v(-273.41, -54.59) * mm, "end": v(-273.3, -49.59) * mm});
            skLineSegment(sketch, "E330.MirrorCS", {"start": v(-249.46, -27) * mm, "end": v(-253.84, -29.4) * mm});
            skLineSegment(sketch, "E331.MirrorCS", {"start": v(-286.84, 30.4) * mm, "end": v(-291.11, 33) * mm});
            skLineSegment(sketch, "E332.MirrorCS", {"start": v(-258.96, 10.4) * mm, "end": v(-263.23, 13) * mm});
            skLineSegment(sketch, "E333.MirrorCS", {"start": v(-277.23, 43) * mm, "end": v(-272.84, 45.4) * mm});
            skLineSegment(sketch, "E334.MirrorCS", {"start": v(-323.27, 70.6) * mm, "end": v(-323.39, 65.6) * mm});
            skLineSegment(sketch, "E335.MirrorCS", {"start": v(-309.96, -49.39) * mm, "end": v(-310.07, -54.39) * mm});
            skLineSegment(sketch, "E336.MirrorCS", {"start": v(-333.8, -56.98) * mm, "end": v(-329.41, -54.58) * mm});
            skLineSegment(sketch, "E337.MirrorCS", {"start": v(-329.3, -34.59) * mm, "end": v(-329.19, -29.59) * mm});
            skLineSegment(sketch, "E338.MirrorCS", {"start": v(-352.07, -54.39) * mm, "end": v(-347.8, -56.98) * mm});
            skLineSegment(sketch, "E339.MirrorCS", {"start": v(-291.34, 23) * mm, "end": v(-286.96, 25.4) * mm});
            skLineSegment(sketch, "E340.MirrorCS", {"start": v(-263.69, -37) * mm, "end": v(-259.3, -34.6) * mm});
            skLineSegment(sketch, "E341.MirrorCS", {"start": v(-239.62, 25.6) * mm, "end": v(-235.34, 23) * mm});
            skLineSegment(sketch, "E342.MirrorCS", {"start": v(-343.3, -49.58) * mm, "end": v(-347.57, -46.99) * mm});
            skLineSegment(sketch, "E343.MirrorCS", {"start": v(-253.84, -14.4) * mm, "end": v(-249.57, -17) * mm});
            skLineSegment(sketch, "E344.MirrorCS", {"start": v(-253.5, 30.6) * mm, "end": v(-253.62, 25.6) * mm});
            skLineSegment(sketch, "E345.MirrorCS", {"start": v(-281.73, 5.6) * mm, "end": v(-277.46, 3) * mm});
            skLineSegment(sketch, "E346.MirrorCS", {"start": v(-244.96, 25.4) * mm, "end": v(-244.84, 30.4) * mm});
            skLineSegment(sketch, "E347.MirrorCS", {"start": v(-342.96, 25.41) * mm, "end": v(-342.84, 30.41) * mm});
            skLineSegment(sketch, "E348.MirrorCS", {"start": v(-240.07, -54.4) * mm, "end": v(-235.8, -57) * mm});
            skLineSegment(sketch, "E349.MirrorCS", {"start": v(-267.5, 45.6) * mm, "end": v(-263.23, 43) * mm});
            skLineSegment(sketch, "E350.MirrorCS", {"start": v(-253.96, -49.4) * mm, "end": v(-254.07, -54.4) * mm});
            skLineSegment(sketch, "E351.MirrorCS", {"start": v(-300.61, 70.4) * mm, "end": v(-304.89, 73) * mm});
            skLineSegment(sketch, "E352.MirrorCS", {"start": v(-273.19, -14.6) * mm, "end": v(-273.07, -9.6) * mm});
            skLineSegment(sketch, "E353.MirrorCS", {"start": v(-295.39, 50.6) * mm, "end": v(-295.5, 45.6) * mm});
            skLineSegment(sketch, "E354.MirrorCS", {"start": v(-263, 53) * mm, "end": v(-267.39, 50.6) * mm});
            skLineSegment(sketch, "E355.MirrorCS", {"start": v(-351.73, 5.61) * mm, "end": v(-347.46, 3.01) * mm});
            skLineSegment(sketch, "E356.MirrorCS", {"start": v(-287.07, -9.6) * mm, "end": v(-291.34, -7) * mm});
            skLineSegment(sketch, "E357.MirrorCS", {"start": v(-254.07, -54.4) * mm, "end": v(-249.8, -56.99) * mm});
            skLineSegment(sketch, "E358.MirrorCS", {"start": v(-253.73, 5.6) * mm, "end": v(-249.46, 3) * mm});
            skLineSegment(sketch, "E359.MirrorCS", {"start": v(-245.07, 5.4) * mm, "end": v(-244.96, 10.4) * mm});
            skLineSegment(sketch, "E360.MirrorCS", {"start": v(-239.5, 45.6) * mm, "end": v(-235.23, 43) * mm});
            skLineSegment(sketch, "E361.MirrorCS", {"start": v(-291.8, -56.99) * mm, "end": v(-287.41, -54.59) * mm});
            skLineSegment(sketch, "E362.MirrorCS", {"start": v(-267.62, 25.6) * mm, "end": v(-263.34, 23) * mm});
            skLineSegment(sketch, "E363.MirrorCS", {"start": v(-323.84, -29.39) * mm, "end": v(-323.96, -34.39) * mm});
            skLineSegment(sketch, "E364.MirrorCS", {"start": v(-258.84, 45.4) * mm, "end": v(-258.73, 50.4) * mm});
            skLineSegment(sketch, "E365.MirrorCS", {"start": v(-272.96, 10.4) * mm, "end": v(-277.23, 13) * mm});
            skLineSegment(sketch, "E366.MirrorCS", {"start": v(-235.69, -37) * mm, "end": v(-231.3, -34.6) * mm});
            skLineSegment(sketch, "E367.MirrorCS", {"start": v(-328.61, 70.4) * mm, "end": v(-332.89, 73) * mm});
            skLineSegment(sketch, "E368.MirrorCS", {"start": v(-328.84, 30.4) * mm, "end": v(-333.11, 33) * mm});
            skLineSegment(sketch, "E369.MirrorCS", {"start": v(-342.84, 30.41) * mm, "end": v(-347.11, 33) * mm});
            skLineSegment(sketch, "E370.MirrorCS", {"start": v(-347.11, 33) * mm, "end": v(-351.5, 30.6) * mm});
            skLineSegment(sketch, "E371.MirrorCS", {"start": v(-295.62, 10.6) * mm, "end": v(-295.73, 5.6) * mm});
            skLineSegment(sketch, "E372.MirrorCS", {"start": v(-305.11, 63) * mm, "end": v(-300.73, 65.4) * mm});
            skLineSegment(sketch, "E373.MirrorCS", {"start": v(-332.89, 73) * mm, "end": v(-337.27, 70.6) * mm});
            skLineSegment(sketch, "E374.MirrorCS", {"start": v(-323.96, -34.39) * mm, "end": v(-319.69, -36.99) * mm});
            skLineSegment(sketch, "E375.MirrorCS", {"start": v(-245.19, -29.6) * mm, "end": v(-249.46, -27) * mm});
            skLineSegment(sketch, "E376.MirrorCS", {"start": v(-253.84, -29.4) * mm, "end": v(-253.96, -34.4) * mm});
            skLineSegment(sketch, "E377.MirrorCS", {"start": v(-295.84, -14.4) * mm, "end": v(-291.57, -16.99) * mm});
            skLineSegment(sketch, "E378.MirrorCS", {"start": v(-249.46, 3) * mm, "end": v(-245.07, 5.4) * mm});
            skLineSegment(sketch, "E379.MirrorCS", {"start": v(-301.3, -49.59) * mm, "end": v(-305.57, -46.99) * mm});
            skLineSegment(sketch, "E380.MirrorCS", {"start": v(-273.19, -29.6) * mm, "end": v(-277.46, -27) * mm});
            skLineSegment(sketch, "E381.MirrorCS", {"start": v(-258.96, 25.4) * mm, "end": v(-258.84, 30.4) * mm});
            skLineSegment(sketch, "E382.MirrorCS", {"start": v(-291.46, -27) * mm, "end": v(-295.84, -29.4) * mm});
            skLineSegment(sketch, "E383.MirrorCS", {"start": v(-259.07, 5.4) * mm, "end": v(-258.96, 10.4) * mm});
            skLineSegment(sketch, "E384.MirrorCS", {"start": v(-281.39, 50.6) * mm, "end": v(-281.5, 45.6) * mm});
            skLineSegment(sketch, "E385.MirrorCS", {"start": v(-319.23, 43) * mm, "end": v(-314.84, 45.4) * mm});
            skLineSegment(sketch, "E386.MirrorCS", {"start": v(-314.61, 70.4) * mm, "end": v(-318.89, 73) * mm});
            skLineSegment(sketch, "E387.MirrorCS", {"start": v(-328.73, 50.4) * mm, "end": v(-333, 53) * mm});
            skLineSegment(sketch, "E388.MirrorCS", {"start": v(-263.23, 43) * mm, "end": v(-258.84, 45.4) * mm});
            skLineSegment(sketch, "E389.MirrorCS", {"start": v(-337.62, 25.6) * mm, "end": v(-333.34, 23.01) * mm});
            skLineSegment(sketch, "E390.MirrorCS", {"start": v(-337.96, -49.39) * mm, "end": v(-338.07, -54.39) * mm});
            skLineSegment(sketch, "E391.MirrorCS", {"start": v(-300.96, 10.4) * mm, "end": v(-305.23, 13) * mm});
            skLineSegment(sketch, "E392.MirrorCS", {"start": v(-287.3, -34.59) * mm, "end": v(-287.19, -29.59) * mm});
            skLineSegment(sketch, "E393.MirrorCS", {"start": v(-305.57, -46.99) * mm, "end": v(-309.96, -49.39) * mm});
            skLineSegment(sketch, "E394.MirrorCS", {"start": v(-301.41, -54.59) * mm, "end": v(-301.3, -49.59) * mm});
            skLineSegment(sketch, "E395.MirrorCS", {"start": v(-291.69, -36.99) * mm, "end": v(-287.3, -34.59) * mm});
            skLineSegment(sketch, "E396.MirrorCS", {"start": v(-309.5, 30.6) * mm, "end": v(-309.62, 25.6) * mm});
            skLineSegment(sketch, "E397.MirrorCS", {"start": v(-309.73, 5.6) * mm, "end": v(-305.46, 3) * mm});
            skLineSegment(sketch, "E398.MirrorCS", {"start": v(-338.07, -54.39) * mm, "end": v(-333.8, -56.98) * mm});
            skLineSegment(sketch, "E399.MirrorCS", {"start": v(-323.73, 5.6) * mm, "end": v(-319.46, 3.01) * mm});
            skLineSegment(sketch, "E400.MirrorCS", {"start": v(-235.46, 3) * mm, "end": v(-231.07, 5.4) * mm});
            skLineSegment(sketch, "E401.MirrorCS", {"start": v(-343.07, 5.41) * mm, "end": v(-342.96, 10.41) * mm});
            skLineSegment(sketch, "E402.MirrorCS", {"start": v(-329.19, -29.59) * mm, "end": v(-333.46, -26.99) * mm});
            skLineSegment(sketch, "E403.MirrorCS", {"start": v(-267.27, 70.6) * mm, "end": v(-267.39, 65.6) * mm});
            skLineSegment(sketch, "E404.MirrorCS", {"start": v(-305.8, -56.99) * mm, "end": v(-301.41, -54.59) * mm});
            skLineSegment(sketch, "E405.MirrorCS", {"start": v(-253.96, -34.4) * mm, "end": v(-249.69, -37) * mm});
            skLineSegment(sketch, "E406.MirrorCS", {"start": v(-231.3, -49.6) * mm, "end": v(-235.57, -47) * mm});
            skLineSegment(sketch, "E407.MirrorCS", {"start": v(-347.46, 3.01) * mm, "end": v(-343.07, 5.41) * mm});
            skLineSegment(sketch, "E408.MirrorCS", {"start": v(-301.19, -29.59) * mm, "end": v(-305.46, -27) * mm});
            skLineSegment(sketch, "E409.MirrorCS", {"start": v(-245.19, -14.6) * mm, "end": v(-245.07, -9.6) * mm});
            skLineSegment(sketch, "E410.MirrorCS", {"start": v(-305, 53) * mm, "end": v(-309.39, 50.6) * mm});
            skPoint(sketch, "E411.MirrorP", {"position": v(-237.25, 64.3) * mm});
            skLineSegment(sketch, "E412", {"start": v(-225, 78) * mm, "end": v(-359.6, 78) * mm});
            skLineSegment(sketch, "E413", {"start": v(-359.6, 78) * mm, "end": v(-361.4, -52.99) * mm});
            skLineSegment(sketch, "E414", {"start": v(-361.4, -52.99) * mm, "end": v(-361.4, -74.99) * mm});
            skLineSegment(sketch, "E415", {"start": v(-361.4, -74.99) * mm, "end": v(-225, -75) * mm});
            skSolve(sketch);
        }
        {
            var Q0;
            Q0=makeQuery(id+"F11.imprint","IMPRINT",FACE,{"disambiguationData":[TD([[makeQuery(id+"F11.imprint","IMPRINT",EDGE,{"derivedFrom":sQuery(id+"F11.wireOp",EDGE,"E28.0")}),1.0]])]});
            var Q1;
            Q1=makeQuery(id+"F11.imprint","IMPRINT",FACE,{"disambiguationData":[TD([[makeQuery(id+"F11.imprint","IMPRINT",EDGE,{"derivedFrom":sQuery(id+"F11.wireOp",EDGE,"E30.MirrorCS")}),-1.0]])]});
            extrude(context, id + "F12", {"entities" : qUnion([Q0, Q1]), "operationType" : NewBodyOperationType.INTERSECT, "endBound" : BoundingType.UP_TO_NEXT, "oppositeDirection" : true, "depth" : 25 * mm, "offsetDistance" : 25 * mm});
        }
    });
